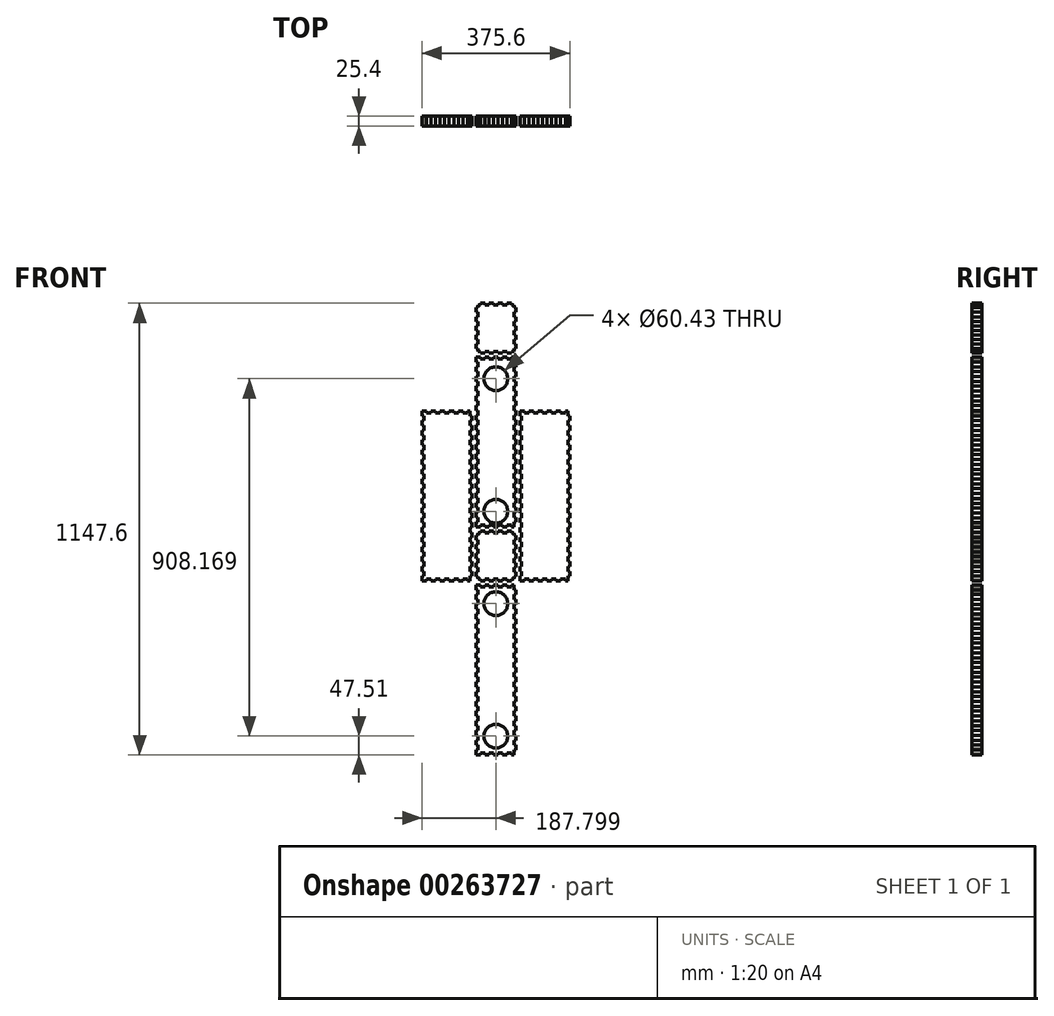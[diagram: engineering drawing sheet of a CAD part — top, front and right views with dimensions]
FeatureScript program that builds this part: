
annotation { "Feature Type Name" : "Feature", "Feature Type Description" : "" }
export const myFeature = defineFeature(function(context is Context, id is Id, definition is map)
    precondition{}
    {
        {
            var Q0;
            Q0=qCreatedBy(makeId("Front.planeOp"),FACE);
            var sketch = newSketch(context, id + "F0", { "sketchPlane" : qUnion([Q0])});
            skLineSegment(sketch, "E0", {"start": v(-50.8, -573.8) * mm, "end": v(-39.51, -573.8) * mm});
            skLineSegment(sketch, "E1", {"start": v(-39.51, -569.04) * mm, "end": v(-39.51, -573.8) * mm});
            skLineSegment(sketch, "E2", {"start": v(-39.51, -569.04) * mm, "end": v(-28.22, -569.04) * mm});
            skLineSegment(sketch, "E3", {"start": v(-28.22, -569.04) * mm, "end": v(-28.22, -573.8) * mm});
            skLineSegment(sketch, "E4", {"start": v(-28.22, -573.8) * mm, "end": v(-16.93, -573.8) * mm});
            skLineSegment(sketch, "E5", {"start": v(-16.93, -569.04) * mm, "end": v(-16.93, -573.8) * mm});
            skLineSegment(sketch, "E6", {"start": v(-16.93, -569.04) * mm, "end": v(-5.65, -569.04) * mm});
            skLineSegment(sketch, "E7", {"start": v(-5.65, -569.04) * mm, "end": v(-5.65, -573.8) * mm});
            skLineSegment(sketch, "E8", {"start": v(-5.65, -573.8) * mm, "end": v(5.64, -573.8) * mm});
            skLineSegment(sketch, "E9", {"start": v(5.64, -569.04) * mm, "end": v(5.64, -573.8) * mm});
            skLineSegment(sketch, "E10", {"start": v(5.64, -569.04) * mm, "end": v(16.93, -569.04) * mm});
            skLineSegment(sketch, "E11", {"start": v(16.93, -569.04) * mm, "end": v(16.93, -573.8) * mm});
            skLineSegment(sketch, "E12", {"start": v(16.93, -573.8) * mm, "end": v(28.22, -573.8) * mm});
            skLineSegment(sketch, "E13", {"start": v(28.22, -569.04) * mm, "end": v(28.22, -573.8) * mm});
            skLineSegment(sketch, "E14", {"start": v(28.22, -569.04) * mm, "end": v(39.51, -569.04) * mm});
            skLineSegment(sketch, "E15", {"start": v(39.51, -569.04) * mm, "end": v(39.51, -573.8) * mm});
            skLineSegment(sketch, "E16", {"start": v(39.51, -573.8) * mm, "end": v(46.04, -573.8) * mm});
            skLineSegment(sketch, "E17", {"start": v(-50.8, -142) * mm, "end": v(-39.51, -142) * mm});
            skLineSegment(sketch, "E18", {"start": v(-39.51, -142) * mm, "end": v(-39.51, -146.76) * mm});
            skLineSegment(sketch, "E19", {"start": v(-39.51, -146.76) * mm, "end": v(-28.22, -146.76) * mm});
            skLineSegment(sketch, "E20", {"start": v(-28.22, -142) * mm, "end": v(-28.22, -146.76) * mm});
            skLineSegment(sketch, "E21", {"start": v(-28.22, -142) * mm, "end": v(-16.93, -142) * mm});
            skLineSegment(sketch, "E22", {"start": v(-16.93, -142) * mm, "end": v(-16.93, -146.76) * mm});
            skLineSegment(sketch, "E23", {"start": v(-16.93, -146.76) * mm, "end": v(-5.65, -146.76) * mm});
            skLineSegment(sketch, "E24", {"start": v(-5.65, -142) * mm, "end": v(-5.65, -146.76) * mm});
            skLineSegment(sketch, "E25", {"start": v(-5.65, -142) * mm, "end": v(5.64, -142) * mm});
            skLineSegment(sketch, "E26", {"start": v(5.64, -142) * mm, "end": v(5.64, -146.76) * mm});
            skLineSegment(sketch, "E27", {"start": v(5.64, -146.76) * mm, "end": v(16.93, -146.76) * mm});
            skLineSegment(sketch, "E28", {"start": v(16.93, -142) * mm, "end": v(16.93, -146.76) * mm});
            skLineSegment(sketch, "E29", {"start": v(16.93, -142) * mm, "end": v(28.22, -142) * mm});
            skLineSegment(sketch, "E30", {"start": v(28.22, -142) * mm, "end": v(28.22, -146.76) * mm});
            skLineSegment(sketch, "E31", {"start": v(28.22, -146.76) * mm, "end": v(39.51, -146.76) * mm});
            skLineSegment(sketch, "E32", {"start": v(39.51, -142) * mm, "end": v(39.51, -146.76) * mm});
            skLineSegment(sketch, "E33", {"start": v(39.51, -142) * mm, "end": v(46.04, -142) * mm});
            skLineSegment(sketch, "E34", {"start": v(-50.8, -573.8) * mm, "end": v(-50.8, -561.46) * mm});
            skLineSegment(sketch, "E35", {"start": v(-46.04, -561.46) * mm, "end": v(-50.8, -561.46) * mm});
            skLineSegment(sketch, "E36", {"start": v(-46.04, -561.46) * mm, "end": v(-46.04, -549.13) * mm});
            skLineSegment(sketch, "E37", {"start": v(-46.04, -549.13) * mm, "end": v(-50.8, -549.13) * mm});
            skLineSegment(sketch, "E38", {"start": v(-50.8, -549.13) * mm, "end": v(-50.8, -536.79) * mm});
            skLineSegment(sketch, "E39", {"start": v(-46.04, -536.79) * mm, "end": v(-50.8, -536.79) * mm});
            skLineSegment(sketch, "E40", {"start": v(-46.04, -536.79) * mm, "end": v(-46.04, -524.45) * mm});
            skLineSegment(sketch, "E41", {"start": v(-46.04, -524.45) * mm, "end": v(-50.8, -524.45) * mm});
            skLineSegment(sketch, "E42", {"start": v(-50.8, -524.45) * mm, "end": v(-50.8, -512.12) * mm});
            skLineSegment(sketch, "E43", {"start": v(-46.04, -512.12) * mm, "end": v(-50.8, -512.12) * mm});
            skLineSegment(sketch, "E44", {"start": v(-46.04, -512.12) * mm, "end": v(-46.04, -499.78) * mm});
            skLineSegment(sketch, "E45", {"start": v(-46.04, -499.78) * mm, "end": v(-50.8, -499.78) * mm});
            skLineSegment(sketch, "E46", {"start": v(-50.8, -499.78) * mm, "end": v(-50.8, -487.44) * mm});
            skLineSegment(sketch, "E47", {"start": v(-46.04, -487.44) * mm, "end": v(-50.8, -487.44) * mm});
            skLineSegment(sketch, "E48", {"start": v(-46.04, -487.44) * mm, "end": v(-46.04, -475.1) * mm});
            skLineSegment(sketch, "E49", {"start": v(-46.04, -475.1) * mm, "end": v(-50.8, -475.1) * mm});
            skLineSegment(sketch, "E50", {"start": v(-50.8, -475.1) * mm, "end": v(-50.8, -462.77) * mm});
            skLineSegment(sketch, "E51", {"start": v(-46.04, -462.77) * mm, "end": v(-50.8, -462.77) * mm});
            skLineSegment(sketch, "E52", {"start": v(-46.04, -462.77) * mm, "end": v(-46.04, -450.43) * mm});
            skLineSegment(sketch, "E53", {"start": v(-46.04, -450.43) * mm, "end": v(-50.8, -450.43) * mm});
            skLineSegment(sketch, "E54", {"start": v(-50.8, -450.43) * mm, "end": v(-50.8, -438.1) * mm});
            skLineSegment(sketch, "E55", {"start": v(-46.04, -438.1) * mm, "end": v(-50.8, -438.1) * mm});
            skLineSegment(sketch, "E56", {"start": v(-46.04, -438.1) * mm, "end": v(-46.04, -425.76) * mm});
            skLineSegment(sketch, "E57", {"start": v(-46.04, -425.76) * mm, "end": v(-50.8, -425.76) * mm});
            skLineSegment(sketch, "E58", {"start": v(-50.8, -425.76) * mm, "end": v(-50.8, -413.42) * mm});
            skLineSegment(sketch, "E59", {"start": v(-46.04, -413.42) * mm, "end": v(-50.8, -413.42) * mm});
            skLineSegment(sketch, "E60", {"start": v(-46.04, -413.42) * mm, "end": v(-46.04, -401.08) * mm});
            skLineSegment(sketch, "E61", {"start": v(-46.04, -401.08) * mm, "end": v(-50.8, -401.08) * mm});
            skLineSegment(sketch, "E62", {"start": v(-50.8, -401.08) * mm, "end": v(-50.8, -388.74) * mm});
            skLineSegment(sketch, "E63", {"start": v(-46.04, -388.74) * mm, "end": v(-50.8, -388.74) * mm});
            skLineSegment(sketch, "E64", {"start": v(-46.04, -388.74) * mm, "end": v(-46.04, -376.4) * mm});
            skLineSegment(sketch, "E65", {"start": v(-46.04, -376.4) * mm, "end": v(-50.8, -376.4) * mm});
            skLineSegment(sketch, "E66", {"start": v(-50.8, -376.4) * mm, "end": v(-50.8, -364.07) * mm});
            skLineSegment(sketch, "E67", {"start": v(-46.04, -364.07) * mm, "end": v(-50.8, -364.07) * mm});
            skLineSegment(sketch, "E68", {"start": v(-46.04, -364.07) * mm, "end": v(-46.04, -351.73) * mm});
            skLineSegment(sketch, "E69", {"start": v(-46.04, -351.73) * mm, "end": v(-50.8, -351.73) * mm});
            skLineSegment(sketch, "E70", {"start": v(-50.8, -351.73) * mm, "end": v(-50.8, -339.4) * mm});
            skLineSegment(sketch, "E71", {"start": v(-46.04, -339.4) * mm, "end": v(-50.8, -339.4) * mm});
            skLineSegment(sketch, "E72", {"start": v(-46.04, -339.4) * mm, "end": v(-46.04, -327.06) * mm});
            skLineSegment(sketch, "E73", {"start": v(-46.04, -327.06) * mm, "end": v(-50.8, -327.06) * mm});
            skLineSegment(sketch, "E74", {"start": v(-50.8, -327.06) * mm, "end": v(-50.8, -314.72) * mm});
            skLineSegment(sketch, "E75", {"start": v(-46.04, -314.72) * mm, "end": v(-50.8, -314.72) * mm});
            skLineSegment(sketch, "E76", {"start": v(-46.04, -314.72) * mm, "end": v(-46.04, -302.38) * mm});
            skLineSegment(sketch, "E77", {"start": v(-46.04, -302.38) * mm, "end": v(-50.8, -302.38) * mm});
            skLineSegment(sketch, "E78", {"start": v(-50.8, -302.38) * mm, "end": v(-50.8, -290.05) * mm});
            skLineSegment(sketch, "E79", {"start": v(-46.04, -290.05) * mm, "end": v(-50.8, -290.05) * mm});
            skLineSegment(sketch, "E80", {"start": v(-46.04, -290.05) * mm, "end": v(-46.04, -277.71) * mm});
            skLineSegment(sketch, "E81", {"start": v(-46.04, -277.71) * mm, "end": v(-50.8, -277.71) * mm});
            skLineSegment(sketch, "E82", {"start": v(-50.8, -277.71) * mm, "end": v(-50.8, -265.37) * mm});
            skLineSegment(sketch, "E83", {"start": v(-46.04, -265.37) * mm, "end": v(-50.8, -265.37) * mm});
            skLineSegment(sketch, "E84", {"start": v(-46.04, -265.37) * mm, "end": v(-46.04, -253.04) * mm});
            skLineSegment(sketch, "E85", {"start": v(-46.04, -253.04) * mm, "end": v(-50.8, -253.04) * mm});
            skLineSegment(sketch, "E86", {"start": v(-50.8, -253.04) * mm, "end": v(-50.8, -240.7) * mm});
            skLineSegment(sketch, "E87", {"start": v(-46.04, -240.7) * mm, "end": v(-50.8, -240.7) * mm});
            skLineSegment(sketch, "E88", {"start": v(-46.04, -240.7) * mm, "end": v(-46.04, -228.36) * mm});
            skLineSegment(sketch, "E89", {"start": v(-46.04, -228.36) * mm, "end": v(-50.8, -228.36) * mm});
            skLineSegment(sketch, "E90", {"start": v(-50.8, -228.36) * mm, "end": v(-50.8, -216.02) * mm});
            skLineSegment(sketch, "E91", {"start": v(-46.04, -216.02) * mm, "end": v(-50.8, -216.02) * mm});
            skLineSegment(sketch, "E92", {"start": v(-46.04, -216.02) * mm, "end": v(-46.04, -203.69) * mm});
            skLineSegment(sketch, "E93", {"start": v(-46.04, -203.69) * mm, "end": v(-50.8, -203.69) * mm});
            skLineSegment(sketch, "E94", {"start": v(-50.8, -203.69) * mm, "end": v(-50.8, -191.35) * mm});
            skLineSegment(sketch, "E95", {"start": v(-46.04, -191.35) * mm, "end": v(-50.8, -191.35) * mm});
            skLineSegment(sketch, "E96", {"start": v(-46.04, -191.35) * mm, "end": v(-46.04, -179.01) * mm});
            skLineSegment(sketch, "E97", {"start": v(-46.04, -179.01) * mm, "end": v(-50.8, -179.01) * mm});
            skLineSegment(sketch, "E98", {"start": v(-50.8, -179.01) * mm, "end": v(-50.8, -166.68) * mm});
            skLineSegment(sketch, "E99", {"start": v(-46.04, -166.68) * mm, "end": v(-50.8, -166.68) * mm});
            skLineSegment(sketch, "E100", {"start": v(-46.04, -166.68) * mm, "end": v(-46.04, -154.34) * mm});
            skLineSegment(sketch, "E101", {"start": v(-46.04, -154.34) * mm, "end": v(-50.8, -154.34) * mm});
            skLineSegment(sketch, "E102", {"start": v(-50.8, -154.34) * mm, "end": v(-50.8, -142) * mm});
            skLineSegment(sketch, "E103", {"start": v(46.04, -573.8) * mm, "end": v(46.04, -561.46) * mm});
            skLineSegment(sketch, "E104", {"start": v(50.8, -561.46) * mm, "end": v(46.04, -561.46) * mm});
            skLineSegment(sketch, "E105", {"start": v(50.8, -561.46) * mm, "end": v(50.8, -549.13) * mm});
            skLineSegment(sketch, "E106", {"start": v(50.8, -549.13) * mm, "end": v(46.04, -549.13) * mm});
            skLineSegment(sketch, "E107", {"start": v(46.04, -549.13) * mm, "end": v(46.04, -536.79) * mm});
            skLineSegment(sketch, "E108", {"start": v(50.8, -536.79) * mm, "end": v(46.04, -536.79) * mm});
            skLineSegment(sketch, "E109", {"start": v(50.8, -536.79) * mm, "end": v(50.8, -524.45) * mm});
            skLineSegment(sketch, "E110", {"start": v(50.8, -524.45) * mm, "end": v(46.04, -524.45) * mm});
            skLineSegment(sketch, "E111", {"start": v(46.04, -524.45) * mm, "end": v(46.04, -512.12) * mm});
            skLineSegment(sketch, "E112", {"start": v(50.8, -512.12) * mm, "end": v(46.04, -512.12) * mm});
            skLineSegment(sketch, "E113", {"start": v(50.8, -512.12) * mm, "end": v(50.8, -499.78) * mm});
            skLineSegment(sketch, "E114", {"start": v(50.8, -499.78) * mm, "end": v(46.04, -499.78) * mm});
            skLineSegment(sketch, "E115", {"start": v(46.04, -499.78) * mm, "end": v(46.04, -487.44) * mm});
            skLineSegment(sketch, "E116", {"start": v(50.8, -487.44) * mm, "end": v(46.04, -487.44) * mm});
            skLineSegment(sketch, "E117", {"start": v(50.8, -487.44) * mm, "end": v(50.8, -475.1) * mm});
            skLineSegment(sketch, "E118", {"start": v(50.8, -475.1) * mm, "end": v(46.04, -475.1) * mm});
            skLineSegment(sketch, "E119", {"start": v(46.04, -475.1) * mm, "end": v(46.04, -462.77) * mm});
            skLineSegment(sketch, "E120", {"start": v(50.8, -462.77) * mm, "end": v(46.04, -462.77) * mm});
            skLineSegment(sketch, "E121", {"start": v(50.8, -462.77) * mm, "end": v(50.8, -450.43) * mm});
            skLineSegment(sketch, "E122", {"start": v(50.8, -450.43) * mm, "end": v(46.04, -450.43) * mm});
            skLineSegment(sketch, "E123", {"start": v(46.04, -450.43) * mm, "end": v(46.04, -438.1) * mm});
            skLineSegment(sketch, "E124", {"start": v(50.8, -438.1) * mm, "end": v(46.04, -438.1) * mm});
            skLineSegment(sketch, "E125", {"start": v(50.8, -438.1) * mm, "end": v(50.8, -425.76) * mm});
            skLineSegment(sketch, "E126", {"start": v(50.8, -425.76) * mm, "end": v(46.04, -425.76) * mm});
            skLineSegment(sketch, "E127", {"start": v(46.04, -425.76) * mm, "end": v(46.04, -413.42) * mm});
            skLineSegment(sketch, "E128", {"start": v(50.8, -413.42) * mm, "end": v(46.04, -413.42) * mm});
            skLineSegment(sketch, "E129", {"start": v(50.8, -413.42) * mm, "end": v(50.8, -401.08) * mm});
            skLineSegment(sketch, "E130", {"start": v(50.8, -401.08) * mm, "end": v(46.04, -401.08) * mm});
            skLineSegment(sketch, "E131", {"start": v(46.04, -401.08) * mm, "end": v(46.04, -388.74) * mm});
            skLineSegment(sketch, "E132", {"start": v(50.8, -388.74) * mm, "end": v(46.04, -388.74) * mm});
            skLineSegment(sketch, "E133", {"start": v(50.8, -388.74) * mm, "end": v(50.8, -376.4) * mm});
            skLineSegment(sketch, "E134", {"start": v(50.8, -376.4) * mm, "end": v(46.04, -376.4) * mm});
            skLineSegment(sketch, "E135", {"start": v(46.04, -376.4) * mm, "end": v(46.04, -364.07) * mm});
            skLineSegment(sketch, "E136", {"start": v(50.8, -364.07) * mm, "end": v(46.04, -364.07) * mm});
            skLineSegment(sketch, "E137", {"start": v(50.8, -364.07) * mm, "end": v(50.8, -351.73) * mm});
            skLineSegment(sketch, "E138", {"start": v(50.8, -351.73) * mm, "end": v(46.04, -351.73) * mm});
            skLineSegment(sketch, "E139", {"start": v(46.04, -351.73) * mm, "end": v(46.04, -339.4) * mm});
            skLineSegment(sketch, "E140", {"start": v(50.8, -339.4) * mm, "end": v(46.04, -339.4) * mm});
            skLineSegment(sketch, "E141", {"start": v(50.8, -339.4) * mm, "end": v(50.8, -327.06) * mm});
            skLineSegment(sketch, "E142", {"start": v(50.8, -327.06) * mm, "end": v(46.04, -327.06) * mm});
            skLineSegment(sketch, "E143", {"start": v(46.04, -327.06) * mm, "end": v(46.04, -314.72) * mm});
            skLineSegment(sketch, "E144", {"start": v(50.8, -314.72) * mm, "end": v(46.04, -314.72) * mm});
            skLineSegment(sketch, "E145", {"start": v(50.8, -314.72) * mm, "end": v(50.8, -302.38) * mm});
            skLineSegment(sketch, "E146", {"start": v(50.8, -302.38) * mm, "end": v(46.04, -302.38) * mm});
            skLineSegment(sketch, "E147", {"start": v(46.04, -302.38) * mm, "end": v(46.04, -290.05) * mm});
            skLineSegment(sketch, "E148", {"start": v(50.8, -290.05) * mm, "end": v(46.04, -290.05) * mm});
            skLineSegment(sketch, "E149", {"start": v(50.8, -290.05) * mm, "end": v(50.8, -277.71) * mm});
            skLineSegment(sketch, "E150", {"start": v(50.8, -277.71) * mm, "end": v(46.04, -277.71) * mm});
            skLineSegment(sketch, "E151", {"start": v(46.04, -277.71) * mm, "end": v(46.04, -265.37) * mm});
            skLineSegment(sketch, "E152", {"start": v(50.8, -265.37) * mm, "end": v(46.04, -265.37) * mm});
            skLineSegment(sketch, "E153", {"start": v(50.8, -265.37) * mm, "end": v(50.8, -253.04) * mm});
            skLineSegment(sketch, "E154", {"start": v(50.8, -253.04) * mm, "end": v(46.04, -253.04) * mm});
            skLineSegment(sketch, "E155", {"start": v(46.04, -253.04) * mm, "end": v(46.04, -240.7) * mm});
            skLineSegment(sketch, "E156", {"start": v(50.8, -240.7) * mm, "end": v(46.04, -240.7) * mm});
            skLineSegment(sketch, "E157", {"start": v(50.8, -240.7) * mm, "end": v(50.8, -228.36) * mm});
            skLineSegment(sketch, "E158", {"start": v(50.8, -228.36) * mm, "end": v(46.04, -228.36) * mm});
            skLineSegment(sketch, "E159", {"start": v(46.04, -228.36) * mm, "end": v(46.04, -216.02) * mm});
            skLineSegment(sketch, "E160", {"start": v(50.8, -216.02) * mm, "end": v(46.04, -216.02) * mm});
            skLineSegment(sketch, "E161", {"start": v(50.8, -216.02) * mm, "end": v(50.8, -203.69) * mm});
            skLineSegment(sketch, "E162", {"start": v(50.8, -203.69) * mm, "end": v(46.04, -203.69) * mm});
            skLineSegment(sketch, "E163", {"start": v(46.04, -203.69) * mm, "end": v(46.04, -191.35) * mm});
            skLineSegment(sketch, "E164", {"start": v(50.8, -191.35) * mm, "end": v(46.04, -191.35) * mm});
            skLineSegment(sketch, "E165", {"start": v(50.8, -191.35) * mm, "end": v(50.8, -179.01) * mm});
            skLineSegment(sketch, "E166", {"start": v(50.8, -179.01) * mm, "end": v(46.04, -179.01) * mm});
            skLineSegment(sketch, "E167", {"start": v(46.04, -179.01) * mm, "end": v(46.04, -166.68) * mm});
            skLineSegment(sketch, "E168", {"start": v(50.8, -166.68) * mm, "end": v(46.04, -166.68) * mm});
            skLineSegment(sketch, "E169", {"start": v(50.8, -166.68) * mm, "end": v(50.8, -154.34) * mm});
            skLineSegment(sketch, "E170", {"start": v(50.8, -154.34) * mm, "end": v(46.04, -154.34) * mm});
            skLineSegment(sketch, "E171", {"start": v(46.04, -154.34) * mm, "end": v(46.04, -142) * mm});
            skLineSegment(sketch, "E172", {"start": v(-187.8, -132) * mm, "end": v(-176.25, -132) * mm});
            skLineSegment(sketch, "E173", {"start": v(-176.25, -127.24) * mm, "end": v(-176.25, -132) * mm});
            skLineSegment(sketch, "E174", {"start": v(-176.25, -127.24) * mm, "end": v(-164.7, -127.24) * mm});
            skLineSegment(sketch, "E175", {"start": v(-164.7, -127.24) * mm, "end": v(-164.7, -132) * mm});
            skLineSegment(sketch, "E176", {"start": v(-164.7, -132) * mm, "end": v(-153.16, -132) * mm});
            skLineSegment(sketch, "E177", {"start": v(-153.16, -127.24) * mm, "end": v(-153.16, -132) * mm});
            skLineSegment(sketch, "E178", {"start": v(-153.16, -127.24) * mm, "end": v(-141.62, -127.24) * mm});
            skLineSegment(sketch, "E179", {"start": v(-141.62, -127.24) * mm, "end": v(-141.62, -132) * mm});
            skLineSegment(sketch, "E180", {"start": v(-141.62, -132) * mm, "end": v(-130.07, -132) * mm});
            skLineSegment(sketch, "E181", {"start": v(-130.07, -127.24) * mm, "end": v(-130.07, -132) * mm});
            skLineSegment(sketch, "E182", {"start": v(-130.07, -127.24) * mm, "end": v(-118.53, -127.24) * mm});
            skLineSegment(sketch, "E183", {"start": v(-118.53, -127.24) * mm, "end": v(-118.53, -132) * mm});
            skLineSegment(sketch, "E184", {"start": v(-118.53, -132) * mm, "end": v(-106.98, -132) * mm});
            skLineSegment(sketch, "E185", {"start": v(-106.98, -127.24) * mm, "end": v(-106.98, -132) * mm});
            skLineSegment(sketch, "E186", {"start": v(-106.98, -127.24) * mm, "end": v(-95.44, -127.24) * mm});
            skLineSegment(sketch, "E187", {"start": v(-95.44, -127.24) * mm, "end": v(-95.44, -132) * mm});
            skLineSegment(sketch, "E188", {"start": v(-95.44, -132) * mm, "end": v(-83.9, -132) * mm});
            skLineSegment(sketch, "E189", {"start": v(-83.9, -127.24) * mm, "end": v(-83.9, -132) * mm});
            skLineSegment(sketch, "E190", {"start": v(-83.9, -127.24) * mm, "end": v(-72.35, -127.24) * mm});
            skLineSegment(sketch, "E191", {"start": v(-72.35, -127.24) * mm, "end": v(-72.35, -132) * mm});
            skLineSegment(sketch, "E192", {"start": v(-72.35, -132) * mm, "end": v(-65.56, -132) * mm});
            skLineSegment(sketch, "E193", {"start": v(-187.8, 299.8) * mm, "end": v(-176.25, 299.8) * mm});
            skLineSegment(sketch, "E194", {"start": v(-176.25, 299.8) * mm, "end": v(-176.25, 295.04) * mm});
            skLineSegment(sketch, "E195", {"start": v(-176.25, 295.04) * mm, "end": v(-164.7, 295.04) * mm});
            skLineSegment(sketch, "E196", {"start": v(-164.7, 299.8) * mm, "end": v(-164.7, 295.04) * mm});
            skLineSegment(sketch, "E197", {"start": v(-164.7, 299.8) * mm, "end": v(-153.16, 299.8) * mm});
            skLineSegment(sketch, "E198", {"start": v(-153.16, 299.8) * mm, "end": v(-153.16, 295.04) * mm});
            skLineSegment(sketch, "E199", {"start": v(-153.16, 295.04) * mm, "end": v(-141.62, 295.04) * mm});
            skLineSegment(sketch, "E200", {"start": v(-141.62, 299.8) * mm, "end": v(-141.62, 295.04) * mm});
            skLineSegment(sketch, "E201", {"start": v(-141.62, 299.8) * mm, "end": v(-130.07, 299.8) * mm});
            skLineSegment(sketch, "E202", {"start": v(-130.07, 299.8) * mm, "end": v(-130.07, 295.04) * mm});
            skLineSegment(sketch, "E203", {"start": v(-130.07, 295.04) * mm, "end": v(-118.53, 295.04) * mm});
            skLineSegment(sketch, "E204", {"start": v(-118.53, 299.8) * mm, "end": v(-118.53, 295.04) * mm});
            skLineSegment(sketch, "E205", {"start": v(-118.53, 299.8) * mm, "end": v(-106.98, 299.8) * mm});
            skLineSegment(sketch, "E206", {"start": v(-106.98, 299.8) * mm, "end": v(-106.98, 295.04) * mm});
            skLineSegment(sketch, "E207", {"start": v(-106.98, 295.04) * mm, "end": v(-95.44, 295.04) * mm});
            skLineSegment(sketch, "E208", {"start": v(-95.44, 299.8) * mm, "end": v(-95.44, 295.04) * mm});
            skLineSegment(sketch, "E209", {"start": v(-95.44, 299.8) * mm, "end": v(-83.9, 299.8) * mm});
            skLineSegment(sketch, "E210", {"start": v(-83.9, 299.8) * mm, "end": v(-83.9, 295.04) * mm});
            skLineSegment(sketch, "E211", {"start": v(-83.9, 295.04) * mm, "end": v(-72.35, 295.04) * mm});
            skLineSegment(sketch, "E212", {"start": v(-72.35, 299.8) * mm, "end": v(-72.35, 295.04) * mm});
            skLineSegment(sketch, "E213", {"start": v(-72.35, 299.8) * mm, "end": v(-65.56, 299.8) * mm});
            skLineSegment(sketch, "E214", {"start": v(-187.8, -132) * mm, "end": v(-187.8, -119.66) * mm});
            skLineSegment(sketch, "E215", {"start": v(-183.04, -119.66) * mm, "end": v(-187.8, -119.66) * mm});
            skLineSegment(sketch, "E216", {"start": v(-183.04, -119.66) * mm, "end": v(-183.04, -107.33) * mm});
            skLineSegment(sketch, "E217", {"start": v(-183.04, -107.33) * mm, "end": v(-187.8, -107.33) * mm});
            skLineSegment(sketch, "E218", {"start": v(-187.8, -107.33) * mm, "end": v(-187.8, -94.99) * mm});
            skLineSegment(sketch, "E219", {"start": v(-183.04, -94.99) * mm, "end": v(-187.8, -94.99) * mm});
            skLineSegment(sketch, "E220", {"start": v(-183.04, -94.99) * mm, "end": v(-183.04, -82.65) * mm});
            skLineSegment(sketch, "E221", {"start": v(-183.04, -82.65) * mm, "end": v(-187.8, -82.65) * mm});
            skLineSegment(sketch, "E222", {"start": v(-187.8, -82.65) * mm, "end": v(-187.8, -70.32) * mm});
            skLineSegment(sketch, "E223", {"start": v(-183.04, -70.32) * mm, "end": v(-187.8, -70.32) * mm});
            skLineSegment(sketch, "E224", {"start": v(-183.04, -70.32) * mm, "end": v(-183.04, -57.98) * mm});
            skLineSegment(sketch, "E225", {"start": v(-183.04, -57.98) * mm, "end": v(-187.8, -57.98) * mm});
            skLineSegment(sketch, "E226", {"start": v(-187.8, -57.98) * mm, "end": v(-187.8, -45.64) * mm});
            skLineSegment(sketch, "E227", {"start": v(-183.04, -45.64) * mm, "end": v(-187.8, -45.64) * mm});
            skLineSegment(sketch, "E228", {"start": v(-183.04, -45.64) * mm, "end": v(-183.04, -33.3) * mm});
            skLineSegment(sketch, "E229", {"start": v(-183.04, -33.3) * mm, "end": v(-187.8, -33.3) * mm});
            skLineSegment(sketch, "E230", {"start": v(-187.8, -33.3) * mm, "end": v(-187.8, -20.97) * mm});
            skLineSegment(sketch, "E231", {"start": v(-183.04, -20.97) * mm, "end": v(-187.8, -20.97) * mm});
            skLineSegment(sketch, "E232", {"start": v(-183.04, -20.97) * mm, "end": v(-183.04, -8.63) * mm});
            skLineSegment(sketch, "E233", {"start": v(-183.04, -8.63) * mm, "end": v(-187.8, -8.63) * mm});
            skLineSegment(sketch, "E234", {"start": v(-187.8, -8.63) * mm, "end": v(-187.8, 3.7) * mm});
            skLineSegment(sketch, "E235", {"start": v(-183.04, 3.7) * mm, "end": v(-187.8, 3.7) * mm});
            skLineSegment(sketch, "E236", {"start": v(-183.04, 3.7) * mm, "end": v(-183.04, 16.04) * mm});
            skLineSegment(sketch, "E237", {"start": v(-183.04, 16.04) * mm, "end": v(-187.8, 16.04) * mm});
            skLineSegment(sketch, "E238", {"start": v(-187.8, 16.04) * mm, "end": v(-187.8, 28.38) * mm});
            skLineSegment(sketch, "E239", {"start": v(-183.04, 28.38) * mm, "end": v(-187.8, 28.38) * mm});
            skLineSegment(sketch, "E240", {"start": v(-183.04, 28.38) * mm, "end": v(-183.04, 40.72) * mm});
            skLineSegment(sketch, "E241", {"start": v(-183.04, 40.72) * mm, "end": v(-187.8, 40.72) * mm});
            skLineSegment(sketch, "E242", {"start": v(-187.8, 40.72) * mm, "end": v(-187.8, 53.06) * mm});
            skLineSegment(sketch, "E243", {"start": v(-183.04, 53.06) * mm, "end": v(-187.8, 53.06) * mm});
            skLineSegment(sketch, "E244", {"start": v(-183.04, 53.06) * mm, "end": v(-183.04, 65.39) * mm});
            skLineSegment(sketch, "E245", {"start": v(-183.04, 65.39) * mm, "end": v(-187.8, 65.39) * mm});
            skLineSegment(sketch, "E246", {"start": v(-187.8, 65.39) * mm, "end": v(-187.8, 77.73) * mm});
            skLineSegment(sketch, "E247", {"start": v(-183.04, 77.73) * mm, "end": v(-187.8, 77.73) * mm});
            skLineSegment(sketch, "E248", {"start": v(-183.04, 77.73) * mm, "end": v(-183.04, 90.07) * mm});
            skLineSegment(sketch, "E249", {"start": v(-183.04, 90.07) * mm, "end": v(-187.8, 90.07) * mm});
            skLineSegment(sketch, "E250", {"start": v(-187.8, 90.07) * mm, "end": v(-187.8, 102.4) * mm});
            skLineSegment(sketch, "E251", {"start": v(-183.04, 102.4) * mm, "end": v(-187.8, 102.4) * mm});
            skLineSegment(sketch, "E252", {"start": v(-183.04, 102.4) * mm, "end": v(-183.04, 114.74) * mm});
            skLineSegment(sketch, "E253", {"start": v(-183.04, 114.74) * mm, "end": v(-187.8, 114.74) * mm});
            skLineSegment(sketch, "E254", {"start": v(-187.8, 114.74) * mm, "end": v(-187.8, 127.08) * mm});
            skLineSegment(sketch, "E255", {"start": v(-183.04, 127.08) * mm, "end": v(-187.8, 127.08) * mm});
            skLineSegment(sketch, "E256", {"start": v(-183.04, 127.08) * mm, "end": v(-183.04, 139.42) * mm});
            skLineSegment(sketch, "E257", {"start": v(-183.04, 139.42) * mm, "end": v(-187.8, 139.42) * mm});
            skLineSegment(sketch, "E258", {"start": v(-187.8, 139.42) * mm, "end": v(-187.8, 151.75) * mm});
            skLineSegment(sketch, "E259", {"start": v(-183.04, 151.75) * mm, "end": v(-187.8, 151.75) * mm});
            skLineSegment(sketch, "E260", {"start": v(-183.04, 151.75) * mm, "end": v(-183.04, 164.1) * mm});
            skLineSegment(sketch, "E261", {"start": v(-183.04, 164.1) * mm, "end": v(-187.8, 164.1) * mm});
            skLineSegment(sketch, "E262", {"start": v(-187.8, 164.1) * mm, "end": v(-187.8, 176.43) * mm});
            skLineSegment(sketch, "E263", {"start": v(-183.04, 176.43) * mm, "end": v(-187.8, 176.43) * mm});
            skLineSegment(sketch, "E264", {"start": v(-183.04, 176.43) * mm, "end": v(-183.04, 188.76) * mm});
            skLineSegment(sketch, "E265", {"start": v(-183.04, 188.76) * mm, "end": v(-187.8, 188.76) * mm});
            skLineSegment(sketch, "E266", {"start": v(-187.8, 188.76) * mm, "end": v(-187.8, 201.1) * mm});
            skLineSegment(sketch, "E267", {"start": v(-183.04, 201.1) * mm, "end": v(-187.8, 201.1) * mm});
            skLineSegment(sketch, "E268", {"start": v(-183.04, 201.1) * mm, "end": v(-183.04, 213.44) * mm});
            skLineSegment(sketch, "E269", {"start": v(-183.04, 213.44) * mm, "end": v(-187.8, 213.44) * mm});
            skLineSegment(sketch, "E270", {"start": v(-187.8, 213.44) * mm, "end": v(-187.8, 225.78) * mm});
            skLineSegment(sketch, "E271", {"start": v(-183.04, 225.78) * mm, "end": v(-187.8, 225.78) * mm});
            skLineSegment(sketch, "E272", {"start": v(-183.04, 225.78) * mm, "end": v(-183.04, 238.11) * mm});
            skLineSegment(sketch, "E273", {"start": v(-183.04, 238.11) * mm, "end": v(-187.8, 238.11) * mm});
            skLineSegment(sketch, "E274", {"start": v(-187.8, 238.11) * mm, "end": v(-187.8, 250.45) * mm});
            skLineSegment(sketch, "E275", {"start": v(-183.04, 250.45) * mm, "end": v(-187.8, 250.45) * mm});
            skLineSegment(sketch, "E276", {"start": v(-183.04, 250.45) * mm, "end": v(-183.04, 262.79) * mm});
            skLineSegment(sketch, "E277", {"start": v(-183.04, 262.79) * mm, "end": v(-187.8, 262.79) * mm});
            skLineSegment(sketch, "E278", {"start": v(-187.8, 262.79) * mm, "end": v(-187.8, 275.12) * mm});
            skLineSegment(sketch, "E279", {"start": v(-183.04, 275.12) * mm, "end": v(-187.8, 275.12) * mm});
            skLineSegment(sketch, "E280", {"start": v(-183.04, 275.12) * mm, "end": v(-183.04, 287.46) * mm});
            skLineSegment(sketch, "E281", {"start": v(-183.04, 287.46) * mm, "end": v(-187.8, 287.46) * mm});
            skLineSegment(sketch, "E282", {"start": v(-187.8, 287.46) * mm, "end": v(-187.8, 299.8) * mm});
            skLineSegment(sketch, "E283", {"start": v(-65.56, -132) * mm, "end": v(-65.56, -119.66) * mm});
            skLineSegment(sketch, "E284", {"start": v(-60.8, -119.66) * mm, "end": v(-65.56, -119.66) * mm});
            skLineSegment(sketch, "E285", {"start": v(-60.8, -119.66) * mm, "end": v(-60.8, -107.33) * mm});
            skLineSegment(sketch, "E286", {"start": v(-60.8, -107.33) * mm, "end": v(-65.56, -107.33) * mm});
            skLineSegment(sketch, "E287", {"start": v(-65.56, -107.33) * mm, "end": v(-65.56, -94.99) * mm});
            skLineSegment(sketch, "E288", {"start": v(-60.8, -94.99) * mm, "end": v(-65.56, -94.99) * mm});
            skLineSegment(sketch, "E289", {"start": v(-60.8, -94.99) * mm, "end": v(-60.8, -82.65) * mm});
            skLineSegment(sketch, "E290", {"start": v(-60.8, -82.65) * mm, "end": v(-65.56, -82.65) * mm});
            skLineSegment(sketch, "E291", {"start": v(-65.56, -82.65) * mm, "end": v(-65.56, -70.32) * mm});
            skLineSegment(sketch, "E292", {"start": v(-60.8, -70.32) * mm, "end": v(-65.56, -70.32) * mm});
            skLineSegment(sketch, "E293", {"start": v(-60.8, -70.32) * mm, "end": v(-60.8, -57.98) * mm});
            skLineSegment(sketch, "E294", {"start": v(-60.8, -57.98) * mm, "end": v(-65.56, -57.98) * mm});
            skLineSegment(sketch, "E295", {"start": v(-65.56, -57.98) * mm, "end": v(-65.56, -45.64) * mm});
            skLineSegment(sketch, "E296", {"start": v(-60.8, -45.64) * mm, "end": v(-65.56, -45.64) * mm});
            skLineSegment(sketch, "E297", {"start": v(-60.8, -45.64) * mm, "end": v(-60.8, -33.3) * mm});
            skLineSegment(sketch, "E298", {"start": v(-60.8, -33.3) * mm, "end": v(-65.56, -33.3) * mm});
            skLineSegment(sketch, "E299", {"start": v(-65.56, -33.3) * mm, "end": v(-65.56, -20.97) * mm});
            skLineSegment(sketch, "E300", {"start": v(-60.8, -20.97) * mm, "end": v(-65.56, -20.97) * mm});
            skLineSegment(sketch, "E301", {"start": v(-60.8, -20.97) * mm, "end": v(-60.8, -8.63) * mm});
            skLineSegment(sketch, "E302", {"start": v(-60.8, -8.63) * mm, "end": v(-65.56, -8.63) * mm});
            skLineSegment(sketch, "E303", {"start": v(-65.56, -8.63) * mm, "end": v(-65.56, 3.7) * mm});
            skLineSegment(sketch, "E304", {"start": v(-60.8, 3.7) * mm, "end": v(-65.56, 3.7) * mm});
            skLineSegment(sketch, "E305", {"start": v(-60.8, 3.7) * mm, "end": v(-60.8, 16.04) * mm});
            skLineSegment(sketch, "E306", {"start": v(-60.8, 16.04) * mm, "end": v(-65.56, 16.04) * mm});
            skLineSegment(sketch, "E307", {"start": v(-65.56, 16.04) * mm, "end": v(-65.56, 28.38) * mm});
            skLineSegment(sketch, "E308", {"start": v(-60.8, 28.38) * mm, "end": v(-65.56, 28.38) * mm});
            skLineSegment(sketch, "E309", {"start": v(-60.8, 28.38) * mm, "end": v(-60.8, 40.72) * mm});
            skLineSegment(sketch, "E310", {"start": v(-60.8, 40.72) * mm, "end": v(-65.56, 40.72) * mm});
            skLineSegment(sketch, "E311", {"start": v(-65.56, 40.72) * mm, "end": v(-65.56, 53.06) * mm});
            skLineSegment(sketch, "E312", {"start": v(-60.8, 53.06) * mm, "end": v(-65.56, 53.06) * mm});
            skLineSegment(sketch, "E313", {"start": v(-60.8, 53.06) * mm, "end": v(-60.8, 65.39) * mm});
            skLineSegment(sketch, "E314", {"start": v(-60.8, 65.39) * mm, "end": v(-65.56, 65.39) * mm});
            skLineSegment(sketch, "E315", {"start": v(-65.56, 65.39) * mm, "end": v(-65.56, 77.73) * mm});
            skLineSegment(sketch, "E316", {"start": v(-60.8, 77.73) * mm, "end": v(-65.56, 77.73) * mm});
            skLineSegment(sketch, "E317", {"start": v(-60.8, 77.73) * mm, "end": v(-60.8, 90.07) * mm});
            skLineSegment(sketch, "E318", {"start": v(-60.8, 90.07) * mm, "end": v(-65.56, 90.07) * mm});
            skLineSegment(sketch, "E319", {"start": v(-65.56, 90.07) * mm, "end": v(-65.56, 102.4) * mm});
            skLineSegment(sketch, "E320", {"start": v(-60.8, 102.4) * mm, "end": v(-65.56, 102.4) * mm});
            skLineSegment(sketch, "E321", {"start": v(-60.8, 102.4) * mm, "end": v(-60.8, 114.74) * mm});
            skLineSegment(sketch, "E322", {"start": v(-60.8, 114.74) * mm, "end": v(-65.56, 114.74) * mm});
            skLineSegment(sketch, "E323", {"start": v(-65.56, 114.74) * mm, "end": v(-65.56, 127.08) * mm});
            skLineSegment(sketch, "E324", {"start": v(-60.8, 127.08) * mm, "end": v(-65.56, 127.08) * mm});
            skLineSegment(sketch, "E325", {"start": v(-60.8, 127.08) * mm, "end": v(-60.8, 139.42) * mm});
            skLineSegment(sketch, "E326", {"start": v(-60.8, 139.42) * mm, "end": v(-65.56, 139.42) * mm});
            skLineSegment(sketch, "E327", {"start": v(-65.56, 139.42) * mm, "end": v(-65.56, 151.75) * mm});
            skLineSegment(sketch, "E328", {"start": v(-60.8, 151.75) * mm, "end": v(-65.56, 151.75) * mm});
            skLineSegment(sketch, "E329", {"start": v(-60.8, 151.75) * mm, "end": v(-60.8, 164.1) * mm});
            skLineSegment(sketch, "E330", {"start": v(-60.8, 164.1) * mm, "end": v(-65.56, 164.1) * mm});
            skLineSegment(sketch, "E331", {"start": v(-65.56, 164.1) * mm, "end": v(-65.56, 176.43) * mm});
            skLineSegment(sketch, "E332", {"start": v(-60.8, 176.43) * mm, "end": v(-65.56, 176.43) * mm});
            skLineSegment(sketch, "E333", {"start": v(-60.8, 176.43) * mm, "end": v(-60.8, 188.76) * mm});
            skLineSegment(sketch, "E334", {"start": v(-60.8, 188.76) * mm, "end": v(-65.56, 188.76) * mm});
            skLineSegment(sketch, "E335", {"start": v(-65.56, 188.76) * mm, "end": v(-65.56, 201.1) * mm});
            skLineSegment(sketch, "E336", {"start": v(-60.8, 201.1) * mm, "end": v(-65.56, 201.1) * mm});
            skLineSegment(sketch, "E337", {"start": v(-60.8, 201.1) * mm, "end": v(-60.8, 213.44) * mm});
            skLineSegment(sketch, "E338", {"start": v(-60.8, 213.44) * mm, "end": v(-65.56, 213.44) * mm});
            skLineSegment(sketch, "E339", {"start": v(-65.56, 213.44) * mm, "end": v(-65.56, 225.78) * mm});
            skLineSegment(sketch, "E340", {"start": v(-60.8, 225.78) * mm, "end": v(-65.56, 225.78) * mm});
            skLineSegment(sketch, "E341", {"start": v(-60.8, 225.78) * mm, "end": v(-60.8, 238.11) * mm});
            skLineSegment(sketch, "E342", {"start": v(-60.8, 238.11) * mm, "end": v(-65.56, 238.11) * mm});
            skLineSegment(sketch, "E343", {"start": v(-65.56, 238.11) * mm, "end": v(-65.56, 250.45) * mm});
            skLineSegment(sketch, "E344", {"start": v(-60.8, 250.45) * mm, "end": v(-65.56, 250.45) * mm});
            skLineSegment(sketch, "E345", {"start": v(-60.8, 250.45) * mm, "end": v(-60.8, 262.79) * mm});
            skLineSegment(sketch, "E346", {"start": v(-60.8, 262.79) * mm, "end": v(-65.56, 262.79) * mm});
            skLineSegment(sketch, "E347", {"start": v(-65.56, 262.79) * mm, "end": v(-65.56, 275.12) * mm});
            skLineSegment(sketch, "E348", {"start": v(-60.8, 275.12) * mm, "end": v(-65.56, 275.12) * mm});
            skLineSegment(sketch, "E349", {"start": v(-60.8, 275.12) * mm, "end": v(-60.8, 287.46) * mm});
            skLineSegment(sketch, "E350", {"start": v(-60.8, 287.46) * mm, "end": v(-65.56, 287.46) * mm});
            skLineSegment(sketch, "E351", {"start": v(-65.56, 287.46) * mm, "end": v(-65.56, 299.8) * mm});
            skLineSegment(sketch, "E352", {"start": v(-46.04, -127.24) * mm, "end": v(-39.51, -127.24) * mm});
            skLineSegment(sketch, "E353", {"start": v(-39.51, -127.24) * mm, "end": v(-39.51, -132) * mm});
            skLineSegment(sketch, "E354", {"start": v(-39.51, -132) * mm, "end": v(-28.22, -132) * mm});
            skLineSegment(sketch, "E355", {"start": v(-28.22, -127.24) * mm, "end": v(-28.22, -132) * mm});
            skLineSegment(sketch, "E356", {"start": v(-28.22, -127.24) * mm, "end": v(-16.93, -127.24) * mm});
            skLineSegment(sketch, "E357", {"start": v(-16.93, -127.24) * mm, "end": v(-16.93, -132) * mm});
            skLineSegment(sketch, "E358", {"start": v(-16.93, -132) * mm, "end": v(-5.65, -132) * mm});
            skLineSegment(sketch, "E359", {"start": v(-5.65, -127.24) * mm, "end": v(-5.65, -132) * mm});
            skLineSegment(sketch, "E360", {"start": v(-5.65, -127.24) * mm, "end": v(5.64, -127.24) * mm});
            skLineSegment(sketch, "E361", {"start": v(5.64, -127.24) * mm, "end": v(5.64, -132) * mm});
            skLineSegment(sketch, "E362", {"start": v(5.64, -132) * mm, "end": v(16.93, -132) * mm});
            skLineSegment(sketch, "E363", {"start": v(16.93, -127.24) * mm, "end": v(16.93, -132) * mm});
            skLineSegment(sketch, "E364", {"start": v(16.93, -127.24) * mm, "end": v(28.22, -127.24) * mm});
            skLineSegment(sketch, "E365", {"start": v(28.22, -127.24) * mm, "end": v(28.22, -132) * mm});
            skLineSegment(sketch, "E366", {"start": v(28.22, -132) * mm, "end": v(39.51, -132) * mm});
            skLineSegment(sketch, "E367", {"start": v(39.51, -127.24) * mm, "end": v(39.51, -132) * mm});
            skLineSegment(sketch, "E368", {"start": v(39.51, -127.24) * mm, "end": v(46.04, -127.24) * mm});
            skLineSegment(sketch, "E369", {"start": v(-46.04, -9.76) * mm, "end": v(-39.51, -9.76) * mm});
            skLineSegment(sketch, "E370", {"start": v(-39.51, -5) * mm, "end": v(-39.51, -9.76) * mm});
            skLineSegment(sketch, "E371", {"start": v(-39.51, -5) * mm, "end": v(-28.22, -5) * mm});
            skLineSegment(sketch, "E372", {"start": v(-28.22, -5) * mm, "end": v(-28.22, -9.76) * mm});
            skLineSegment(sketch, "E373", {"start": v(-28.22, -9.76) * mm, "end": v(-16.93, -9.76) * mm});
            skLineSegment(sketch, "E374", {"start": v(-16.93, -5) * mm, "end": v(-16.93, -9.76) * mm});
            skLineSegment(sketch, "E375", {"start": v(-16.93, -5) * mm, "end": v(-5.65, -5) * mm});
            skLineSegment(sketch, "E376", {"start": v(-5.65, -5) * mm, "end": v(-5.65, -9.76) * mm});
            skLineSegment(sketch, "E377", {"start": v(-5.65, -9.76) * mm, "end": v(5.64, -9.76) * mm});
            skLineSegment(sketch, "E378", {"start": v(5.64, -5) * mm, "end": v(5.64, -9.76) * mm});
            skLineSegment(sketch, "E379", {"start": v(5.64, -5) * mm, "end": v(16.93, -5) * mm});
            skLineSegment(sketch, "E380", {"start": v(16.93, -5) * mm, "end": v(16.93, -9.76) * mm});
            skLineSegment(sketch, "E381", {"start": v(16.93, -9.76) * mm, "end": v(28.22, -9.76) * mm});
            skLineSegment(sketch, "E382", {"start": v(28.22, -5) * mm, "end": v(28.22, -9.76) * mm});
            skLineSegment(sketch, "E383", {"start": v(28.22, -5) * mm, "end": v(39.51, -5) * mm});
            skLineSegment(sketch, "E384", {"start": v(39.51, -5) * mm, "end": v(39.51, -9.76) * mm});
            skLineSegment(sketch, "E385", {"start": v(39.51, -9.76) * mm, "end": v(46.04, -9.76) * mm});
            skLineSegment(sketch, "E386", {"start": v(-46.04, -127.24) * mm, "end": v(-46.04, -120.46) * mm});
            skLineSegment(sketch, "E387", {"start": v(-46.04, -120.46) * mm, "end": v(-50.8, -120.46) * mm});
            skLineSegment(sketch, "E388", {"start": v(-50.8, -120.46) * mm, "end": v(-50.8, -108.91) * mm});
            skLineSegment(sketch, "E389", {"start": v(-46.04, -108.91) * mm, "end": v(-50.8, -108.91) * mm});
            skLineSegment(sketch, "E390", {"start": v(-46.04, -108.91) * mm, "end": v(-46.04, -97.36) * mm});
            skLineSegment(sketch, "E391", {"start": v(-46.04, -97.36) * mm, "end": v(-50.8, -97.36) * mm});
            skLineSegment(sketch, "E392", {"start": v(-50.8, -97.36) * mm, "end": v(-50.8, -85.82) * mm});
            skLineSegment(sketch, "E393", {"start": v(-46.04, -85.82) * mm, "end": v(-50.8, -85.82) * mm});
            skLineSegment(sketch, "E394", {"start": v(-46.04, -85.82) * mm, "end": v(-46.04, -74.27) * mm});
            skLineSegment(sketch, "E395", {"start": v(-46.04, -74.27) * mm, "end": v(-50.8, -74.27) * mm});
            skLineSegment(sketch, "E396", {"start": v(-50.8, -74.27) * mm, "end": v(-50.8, -62.73) * mm});
            skLineSegment(sketch, "E397", {"start": v(-46.04, -62.73) * mm, "end": v(-50.8, -62.73) * mm});
            skLineSegment(sketch, "E398", {"start": v(-46.04, -62.73) * mm, "end": v(-46.04, -51.18) * mm});
            skLineSegment(sketch, "E399", {"start": v(-46.04, -51.18) * mm, "end": v(-50.8, -51.18) * mm});
            skLineSegment(sketch, "E400", {"start": v(-50.8, -51.18) * mm, "end": v(-50.8, -39.64) * mm});
            skLineSegment(sketch, "E401", {"start": v(-46.04, -39.64) * mm, "end": v(-50.8, -39.64) * mm});
            skLineSegment(sketch, "E402", {"start": v(-46.04, -39.64) * mm, "end": v(-46.04, -28.1) * mm});
            skLineSegment(sketch, "E403", {"start": v(-46.04, -28.1) * mm, "end": v(-50.8, -28.1) * mm});
            skLineSegment(sketch, "E404", {"start": v(-50.8, -28.1) * mm, "end": v(-50.8, -16.55) * mm});
            skLineSegment(sketch, "E405", {"start": v(-46.04, -16.55) * mm, "end": v(-50.8, -16.55) * mm});
            skLineSegment(sketch, "E406", {"start": v(-46.04, -16.55) * mm, "end": v(-46.04, -9.76) * mm});
            skLineSegment(sketch, "E407", {"start": v(46.04, -127.24) * mm, "end": v(46.04, -120.46) * mm});
            skLineSegment(sketch, "E408", {"start": v(50.8, -120.46) * mm, "end": v(46.04, -120.46) * mm});
            skLineSegment(sketch, "E409", {"start": v(50.8, -120.46) * mm, "end": v(50.8, -108.91) * mm});
            skLineSegment(sketch, "E410", {"start": v(50.8, -108.91) * mm, "end": v(46.04, -108.91) * mm});
            skLineSegment(sketch, "E411", {"start": v(46.04, -108.91) * mm, "end": v(46.04, -97.36) * mm});
            skLineSegment(sketch, "E412", {"start": v(50.8, -97.36) * mm, "end": v(46.04, -97.36) * mm});
            skLineSegment(sketch, "E413", {"start": v(50.8, -97.36) * mm, "end": v(50.8, -85.82) * mm});
            skLineSegment(sketch, "E414", {"start": v(50.8, -85.82) * mm, "end": v(46.04, -85.82) * mm});
            skLineSegment(sketch, "E415", {"start": v(46.04, -85.82) * mm, "end": v(46.04, -74.27) * mm});
            skLineSegment(sketch, "E416", {"start": v(50.8, -74.27) * mm, "end": v(46.04, -74.27) * mm});
            skLineSegment(sketch, "E417", {"start": v(50.8, -74.27) * mm, "end": v(50.8, -62.73) * mm});
            skLineSegment(sketch, "E418", {"start": v(50.8, -62.73) * mm, "end": v(46.04, -62.73) * mm});
            skLineSegment(sketch, "E419", {"start": v(46.04, -62.73) * mm, "end": v(46.04, -51.18) * mm});
            skLineSegment(sketch, "E420", {"start": v(50.8, -51.18) * mm, "end": v(46.04, -51.18) * mm});
            skLineSegment(sketch, "E421", {"start": v(50.8, -51.18) * mm, "end": v(50.8, -39.64) * mm});
            skLineSegment(sketch, "E422", {"start": v(50.8, -39.64) * mm, "end": v(46.04, -39.64) * mm});
            skLineSegment(sketch, "E423", {"start": v(46.04, -39.64) * mm, "end": v(46.04, -28.1) * mm});
            skLineSegment(sketch, "E424", {"start": v(50.8, -28.1) * mm, "end": v(46.04, -28.1) * mm});
            skLineSegment(sketch, "E425", {"start": v(50.8, -28.1) * mm, "end": v(50.8, -16.55) * mm});
            skLineSegment(sketch, "E426", {"start": v(50.8, -16.55) * mm, "end": v(46.04, -16.55) * mm});
            skLineSegment(sketch, "E427", {"start": v(46.04, -16.55) * mm, "end": v(46.04, -9.76) * mm});
            skLineSegment(sketch, "E428", {"start": v(60.8, -132) * mm, "end": v(72.34, -132) * mm});
            skLineSegment(sketch, "E429", {"start": v(72.34, -127.24) * mm, "end": v(72.34, -132) * mm});
            skLineSegment(sketch, "E430", {"start": v(72.34, -127.24) * mm, "end": v(83.9, -127.24) * mm});
            skLineSegment(sketch, "E431", {"start": v(83.9, -127.24) * mm, "end": v(83.9, -132) * mm});
            skLineSegment(sketch, "E432", {"start": v(83.9, -132) * mm, "end": v(95.44, -132) * mm});
            skLineSegment(sketch, "E433", {"start": v(95.44, -127.24) * mm, "end": v(95.44, -132) * mm});
            skLineSegment(sketch, "E434", {"start": v(95.44, -127.24) * mm, "end": v(106.98, -127.24) * mm});
            skLineSegment(sketch, "E435", {"start": v(106.98, -127.24) * mm, "end": v(106.98, -132) * mm});
            skLineSegment(sketch, "E436", {"start": v(106.98, -132) * mm, "end": v(118.53, -132) * mm});
            skLineSegment(sketch, "E437", {"start": v(118.53, -127.24) * mm, "end": v(118.53, -132) * mm});
            skLineSegment(sketch, "E438", {"start": v(118.53, -127.24) * mm, "end": v(130.07, -127.24) * mm});
            skLineSegment(sketch, "E439", {"start": v(130.07, -127.24) * mm, "end": v(130.07, -132) * mm});
            skLineSegment(sketch, "E440", {"start": v(130.07, -132) * mm, "end": v(141.62, -132) * mm});
            skLineSegment(sketch, "E441", {"start": v(141.62, -127.24) * mm, "end": v(141.62, -132) * mm});
            skLineSegment(sketch, "E442", {"start": v(141.62, -127.24) * mm, "end": v(153.16, -127.24) * mm});
            skLineSegment(sketch, "E443", {"start": v(153.16, -127.24) * mm, "end": v(153.16, -132) * mm});
            skLineSegment(sketch, "E444", {"start": v(153.16, -132) * mm, "end": v(164.71, -132) * mm});
            skLineSegment(sketch, "E445", {"start": v(164.71, -127.24) * mm, "end": v(164.71, -132) * mm});
            skLineSegment(sketch, "E446", {"start": v(164.71, -127.24) * mm, "end": v(176.25, -127.24) * mm});
            skLineSegment(sketch, "E447", {"start": v(176.25, -127.24) * mm, "end": v(176.25, -132) * mm});
            skLineSegment(sketch, "E448", {"start": v(176.25, -132) * mm, "end": v(183.04, -132) * mm});
            skLineSegment(sketch, "E449", {"start": v(60.8, 299.8) * mm, "end": v(72.34, 299.8) * mm});
            skLineSegment(sketch, "E450", {"start": v(72.34, 299.8) * mm, "end": v(72.34, 295.04) * mm});
            skLineSegment(sketch, "E451", {"start": v(72.34, 295.04) * mm, "end": v(83.9, 295.04) * mm});
            skLineSegment(sketch, "E452", {"start": v(83.9, 299.8) * mm, "end": v(83.9, 295.04) * mm});
            skLineSegment(sketch, "E453", {"start": v(83.9, 299.8) * mm, "end": v(95.44, 299.8) * mm});
            skLineSegment(sketch, "E454", {"start": v(95.44, 299.8) * mm, "end": v(95.44, 295.04) * mm});
            skLineSegment(sketch, "E455", {"start": v(95.44, 295.04) * mm, "end": v(106.98, 295.04) * mm});
            skLineSegment(sketch, "E456", {"start": v(106.98, 299.8) * mm, "end": v(106.98, 295.04) * mm});
            skLineSegment(sketch, "E457", {"start": v(106.98, 299.8) * mm, "end": v(118.53, 299.8) * mm});
            skLineSegment(sketch, "E458", {"start": v(118.53, 299.8) * mm, "end": v(118.53, 295.04) * mm});
            skLineSegment(sketch, "E459", {"start": v(118.53, 295.04) * mm, "end": v(130.07, 295.04) * mm});
            skLineSegment(sketch, "E460", {"start": v(130.07, 299.8) * mm, "end": v(130.07, 295.04) * mm});
            skLineSegment(sketch, "E461", {"start": v(130.07, 299.8) * mm, "end": v(141.62, 299.8) * mm});
            skLineSegment(sketch, "E462", {"start": v(141.62, 299.8) * mm, "end": v(141.62, 295.04) * mm});
            skLineSegment(sketch, "E463", {"start": v(141.62, 295.04) * mm, "end": v(153.16, 295.04) * mm});
            skLineSegment(sketch, "E464", {"start": v(153.16, 299.8) * mm, "end": v(153.16, 295.04) * mm});
            skLineSegment(sketch, "E465", {"start": v(153.16, 299.8) * mm, "end": v(164.71, 299.8) * mm});
            skLineSegment(sketch, "E466", {"start": v(164.71, 299.8) * mm, "end": v(164.71, 295.04) * mm});
            skLineSegment(sketch, "E467", {"start": v(164.71, 295.04) * mm, "end": v(176.25, 295.04) * mm});
            skLineSegment(sketch, "E468", {"start": v(176.25, 299.8) * mm, "end": v(176.25, 295.04) * mm});
            skLineSegment(sketch, "E469", {"start": v(176.25, 299.8) * mm, "end": v(183.04, 299.8) * mm});
            skLineSegment(sketch, "E470", {"start": v(60.8, -132) * mm, "end": v(60.8, -119.66) * mm});
            skLineSegment(sketch, "E471", {"start": v(65.56, -119.66) * mm, "end": v(60.8, -119.66) * mm});
            skLineSegment(sketch, "E472", {"start": v(65.56, -119.66) * mm, "end": v(65.56, -107.33) * mm});
            skLineSegment(sketch, "E473", {"start": v(65.56, -107.33) * mm, "end": v(60.8, -107.33) * mm});
            skLineSegment(sketch, "E474", {"start": v(60.8, -107.33) * mm, "end": v(60.8, -94.99) * mm});
            skLineSegment(sketch, "E475", {"start": v(65.56, -94.99) * mm, "end": v(60.8, -94.99) * mm});
            skLineSegment(sketch, "E476", {"start": v(65.56, -94.99) * mm, "end": v(65.56, -82.65) * mm});
            skLineSegment(sketch, "E477", {"start": v(65.56, -82.65) * mm, "end": v(60.8, -82.65) * mm});
            skLineSegment(sketch, "E478", {"start": v(60.8, -82.65) * mm, "end": v(60.8, -70.32) * mm});
            skLineSegment(sketch, "E479", {"start": v(65.56, -70.32) * mm, "end": v(60.8, -70.32) * mm});
            skLineSegment(sketch, "E480", {"start": v(65.56, -70.32) * mm, "end": v(65.56, -57.98) * mm});
            skLineSegment(sketch, "E481", {"start": v(65.56, -57.98) * mm, "end": v(60.8, -57.98) * mm});
            skLineSegment(sketch, "E482", {"start": v(60.8, -57.98) * mm, "end": v(60.8, -45.64) * mm});
            skLineSegment(sketch, "E483", {"start": v(65.56, -45.64) * mm, "end": v(60.8, -45.64) * mm});
            skLineSegment(sketch, "E484", {"start": v(65.56, -45.64) * mm, "end": v(65.56, -33.3) * mm});
            skLineSegment(sketch, "E485", {"start": v(65.56, -33.3) * mm, "end": v(60.8, -33.3) * mm});
            skLineSegment(sketch, "E486", {"start": v(60.8, -33.3) * mm, "end": v(60.8, -20.97) * mm});
            skLineSegment(sketch, "E487", {"start": v(65.56, -20.97) * mm, "end": v(60.8, -20.97) * mm});
            skLineSegment(sketch, "E488", {"start": v(65.56, -20.97) * mm, "end": v(65.56, -8.63) * mm});
            skLineSegment(sketch, "E489", {"start": v(65.56, -8.63) * mm, "end": v(60.8, -8.63) * mm});
            skLineSegment(sketch, "E490", {"start": v(60.8, -8.63) * mm, "end": v(60.8, 3.7) * mm});
            skLineSegment(sketch, "E491", {"start": v(65.56, 3.7) * mm, "end": v(60.8, 3.7) * mm});
            skLineSegment(sketch, "E492", {"start": v(65.56, 3.7) * mm, "end": v(65.56, 16.04) * mm});
            skLineSegment(sketch, "E493", {"start": v(65.56, 16.04) * mm, "end": v(60.8, 16.04) * mm});
            skLineSegment(sketch, "E494", {"start": v(60.8, 16.04) * mm, "end": v(60.8, 28.38) * mm});
            skLineSegment(sketch, "E495", {"start": v(65.56, 28.38) * mm, "end": v(60.8, 28.38) * mm});
            skLineSegment(sketch, "E496", {"start": v(65.56, 28.38) * mm, "end": v(65.56, 40.72) * mm});
            skLineSegment(sketch, "E497", {"start": v(65.56, 40.72) * mm, "end": v(60.8, 40.72) * mm});
            skLineSegment(sketch, "E498", {"start": v(60.8, 40.72) * mm, "end": v(60.8, 53.06) * mm});
            skLineSegment(sketch, "E499", {"start": v(65.56, 53.06) * mm, "end": v(60.8, 53.06) * mm});
            skLineSegment(sketch, "E500", {"start": v(65.56, 53.06) * mm, "end": v(65.56, 65.39) * mm});
            skLineSegment(sketch, "E501", {"start": v(65.56, 65.39) * mm, "end": v(60.8, 65.39) * mm});
            skLineSegment(sketch, "E502", {"start": v(60.8, 65.39) * mm, "end": v(60.8, 77.73) * mm});
            skLineSegment(sketch, "E503", {"start": v(65.56, 77.73) * mm, "end": v(60.8, 77.73) * mm});
            skLineSegment(sketch, "E504", {"start": v(65.56, 77.73) * mm, "end": v(65.56, 90.07) * mm});
            skLineSegment(sketch, "E505", {"start": v(60.8, 90.07) * mm, "end": v(60.8, 102.4) * mm});
            skLineSegment(sketch, "E506", {"start": v(65.56, 102.4) * mm, "end": v(60.8, 102.4) * mm});
            skLineSegment(sketch, "E507", {"start": v(65.56, 102.4) * mm, "end": v(65.56, 114.74) * mm});
            skLineSegment(sketch, "E508", {"start": v(65.56, 114.74) * mm, "end": v(60.8, 114.74) * mm});
            skLineSegment(sketch, "E509", {"start": v(60.8, 114.74) * mm, "end": v(60.8, 127.08) * mm});
            skLineSegment(sketch, "E510", {"start": v(65.56, 127.08) * mm, "end": v(60.8, 127.08) * mm});
            skLineSegment(sketch, "E511", {"start": v(65.56, 127.08) * mm, "end": v(65.56, 139.42) * mm});
            skLineSegment(sketch, "E512", {"start": v(65.56, 139.42) * mm, "end": v(60.8, 139.42) * mm});
            skLineSegment(sketch, "E513", {"start": v(60.8, 139.42) * mm, "end": v(60.8, 151.75) * mm});
            skLineSegment(sketch, "E514", {"start": v(65.56, 151.75) * mm, "end": v(60.8, 151.75) * mm});
            skLineSegment(sketch, "E515", {"start": v(65.56, 151.75) * mm, "end": v(65.56, 164.1) * mm});
            skLineSegment(sketch, "E516", {"start": v(65.56, 164.1) * mm, "end": v(60.8, 164.1) * mm});
            skLineSegment(sketch, "E517", {"start": v(60.8, 164.1) * mm, "end": v(60.8, 176.43) * mm});
            skLineSegment(sketch, "E518", {"start": v(65.56, 176.43) * mm, "end": v(60.8, 176.43) * mm});
            skLineSegment(sketch, "E519", {"start": v(65.56, 176.43) * mm, "end": v(65.56, 188.76) * mm});
            skLineSegment(sketch, "E520", {"start": v(65.56, 188.76) * mm, "end": v(60.8, 188.76) * mm});
            skLineSegment(sketch, "E521", {"start": v(60.8, 188.76) * mm, "end": v(60.8, 201.1) * mm});
            skLineSegment(sketch, "E522", {"start": v(65.56, 201.1) * mm, "end": v(60.8, 201.1) * mm});
            skLineSegment(sketch, "E523", {"start": v(65.56, 201.1) * mm, "end": v(65.56, 213.44) * mm});
            skLineSegment(sketch, "E524", {"start": v(65.56, 213.44) * mm, "end": v(60.8, 213.44) * mm});
            skLineSegment(sketch, "E525", {"start": v(60.8, 213.44) * mm, "end": v(60.8, 225.78) * mm});
            skLineSegment(sketch, "E526", {"start": v(65.56, 225.78) * mm, "end": v(60.8, 225.78) * mm});
            skLineSegment(sketch, "E527", {"start": v(65.56, 225.78) * mm, "end": v(65.56, 238.11) * mm});
            skLineSegment(sketch, "E528", {"start": v(65.56, 238.11) * mm, "end": v(60.8, 238.11) * mm});
            skLineSegment(sketch, "E529", {"start": v(60.8, 238.11) * mm, "end": v(60.8, 250.45) * mm});
            skLineSegment(sketch, "E530", {"start": v(65.56, 250.45) * mm, "end": v(60.8, 250.45) * mm});
            skLineSegment(sketch, "E531", {"start": v(65.56, 250.45) * mm, "end": v(65.56, 262.79) * mm});
            skLineSegment(sketch, "E532", {"start": v(65.56, 262.79) * mm, "end": v(60.8, 262.79) * mm});
            skLineSegment(sketch, "E533", {"start": v(60.8, 262.79) * mm, "end": v(60.8, 275.12) * mm});
            skLineSegment(sketch, "E534", {"start": v(65.56, 275.12) * mm, "end": v(60.8, 275.12) * mm});
            skLineSegment(sketch, "E535", {"start": v(65.56, 275.12) * mm, "end": v(65.56, 287.46) * mm});
            skLineSegment(sketch, "E536", {"start": v(65.56, 287.46) * mm, "end": v(60.8, 287.46) * mm});
            skLineSegment(sketch, "E537", {"start": v(60.8, 287.46) * mm, "end": v(60.8, 299.8) * mm});
            skLineSegment(sketch, "E538", {"start": v(183.04, -132) * mm, "end": v(183.04, -119.66) * mm});
            skLineSegment(sketch, "E539", {"start": v(187.8, -119.66) * mm, "end": v(183.04, -119.66) * mm});
            skLineSegment(sketch, "E540", {"start": v(187.8, -119.66) * mm, "end": v(187.8, -107.33) * mm});
            skLineSegment(sketch, "E541", {"start": v(187.8, -107.33) * mm, "end": v(183.04, -107.33) * mm});
            skLineSegment(sketch, "E542", {"start": v(183.04, -107.33) * mm, "end": v(183.04, -94.99) * mm});
            skLineSegment(sketch, "E543", {"start": v(187.8, -94.99) * mm, "end": v(183.04, -94.99) * mm});
            skLineSegment(sketch, "E544", {"start": v(187.8, -94.99) * mm, "end": v(187.8, -82.65) * mm});
            skLineSegment(sketch, "E545", {"start": v(187.8, -82.65) * mm, "end": v(183.04, -82.65) * mm});
            skLineSegment(sketch, "E546", {"start": v(183.04, -82.65) * mm, "end": v(183.04, -70.32) * mm});
            skLineSegment(sketch, "E547", {"start": v(187.8, -70.32) * mm, "end": v(183.04, -70.32) * mm});
            skLineSegment(sketch, "E548", {"start": v(187.8, -70.32) * mm, "end": v(187.8, -57.98) * mm});
            skLineSegment(sketch, "E549", {"start": v(187.8, -57.98) * mm, "end": v(183.04, -57.98) * mm});
            skLineSegment(sketch, "E550", {"start": v(183.04, -57.98) * mm, "end": v(183.04, -45.64) * mm});
            skLineSegment(sketch, "E551", {"start": v(187.8, -45.64) * mm, "end": v(183.04, -45.64) * mm});
            skLineSegment(sketch, "E552", {"start": v(187.8, -45.64) * mm, "end": v(187.8, -33.3) * mm});
            skLineSegment(sketch, "E553", {"start": v(187.8, -33.3) * mm, "end": v(183.04, -33.3) * mm});
            skLineSegment(sketch, "E554", {"start": v(183.04, -33.3) * mm, "end": v(183.04, -20.97) * mm});
            skLineSegment(sketch, "E555", {"start": v(187.8, -20.97) * mm, "end": v(183.04, -20.97) * mm});
            skLineSegment(sketch, "E556", {"start": v(187.8, -20.97) * mm, "end": v(187.8, -8.63) * mm});
            skLineSegment(sketch, "E557", {"start": v(187.8, -8.63) * mm, "end": v(183.04, -8.63) * mm});
            skLineSegment(sketch, "E558", {"start": v(183.04, -8.63) * mm, "end": v(183.04, 3.7) * mm});
            skLineSegment(sketch, "E559", {"start": v(187.8, 3.7) * mm, "end": v(183.04, 3.7) * mm});
            skLineSegment(sketch, "E560", {"start": v(187.8, 3.7) * mm, "end": v(187.8, 16.04) * mm});
            skLineSegment(sketch, "E561", {"start": v(187.8, 16.04) * mm, "end": v(183.04, 16.04) * mm});
            skLineSegment(sketch, "E562", {"start": v(183.04, 16.04) * mm, "end": v(183.04, 28.38) * mm});
            skLineSegment(sketch, "E563", {"start": v(187.8, 28.38) * mm, "end": v(183.04, 28.38) * mm});
            skLineSegment(sketch, "E564", {"start": v(187.8, 28.38) * mm, "end": v(187.8, 40.72) * mm});
            skLineSegment(sketch, "E565", {"start": v(187.8, 40.72) * mm, "end": v(183.04, 40.72) * mm});
            skLineSegment(sketch, "E566", {"start": v(183.04, 40.72) * mm, "end": v(183.04, 53.06) * mm});
            skLineSegment(sketch, "E567", {"start": v(187.8, 53.06) * mm, "end": v(183.04, 53.06) * mm});
            skLineSegment(sketch, "E568", {"start": v(187.8, 53.06) * mm, "end": v(187.8, 65.39) * mm});
            skLineSegment(sketch, "E569", {"start": v(187.8, 65.39) * mm, "end": v(183.04, 65.39) * mm});
            skLineSegment(sketch, "E570", {"start": v(183.04, 65.39) * mm, "end": v(183.04, 77.73) * mm});
            skLineSegment(sketch, "E571", {"start": v(187.8, 77.73) * mm, "end": v(183.04, 77.73) * mm});
            skLineSegment(sketch, "E572", {"start": v(187.8, 77.73) * mm, "end": v(187.8, 90.07) * mm});
            skLineSegment(sketch, "E573", {"start": v(187.8, 90.07) * mm, "end": v(183.04, 90.07) * mm});
            skLineSegment(sketch, "E574", {"start": v(183.04, 90.07) * mm, "end": v(183.04, 102.4) * mm});
            skLineSegment(sketch, "E575", {"start": v(187.8, 102.4) * mm, "end": v(183.04, 102.4) * mm});
            skLineSegment(sketch, "E576", {"start": v(187.8, 102.4) * mm, "end": v(187.8, 114.74) * mm});
            skLineSegment(sketch, "E577", {"start": v(187.8, 114.74) * mm, "end": v(183.04, 114.74) * mm});
            skLineSegment(sketch, "E578", {"start": v(183.04, 114.74) * mm, "end": v(183.04, 127.08) * mm});
            skLineSegment(sketch, "E579", {"start": v(187.8, 127.08) * mm, "end": v(183.04, 127.08) * mm});
            skLineSegment(sketch, "E580", {"start": v(187.8, 127.08) * mm, "end": v(187.8, 139.42) * mm});
            skLineSegment(sketch, "E581", {"start": v(187.8, 139.42) * mm, "end": v(183.04, 139.42) * mm});
            skLineSegment(sketch, "E582", {"start": v(183.04, 139.42) * mm, "end": v(183.04, 151.75) * mm});
            skLineSegment(sketch, "E583", {"start": v(187.8, 151.75) * mm, "end": v(183.04, 151.75) * mm});
            skLineSegment(sketch, "E584", {"start": v(187.8, 151.75) * mm, "end": v(187.8, 164.1) * mm});
            skLineSegment(sketch, "E585", {"start": v(187.8, 164.1) * mm, "end": v(183.04, 164.1) * mm});
            skLineSegment(sketch, "E586", {"start": v(183.04, 164.1) * mm, "end": v(183.04, 176.43) * mm});
            skLineSegment(sketch, "E587", {"start": v(187.8, 176.43) * mm, "end": v(183.04, 176.43) * mm});
            skLineSegment(sketch, "E588", {"start": v(187.8, 176.43) * mm, "end": v(187.8, 188.76) * mm});
            skLineSegment(sketch, "E589", {"start": v(187.8, 188.76) * mm, "end": v(183.04, 188.76) * mm});
            skLineSegment(sketch, "E590", {"start": v(183.04, 188.76) * mm, "end": v(183.04, 201.1) * mm});
            skLineSegment(sketch, "E591", {"start": v(187.8, 201.1) * mm, "end": v(183.04, 201.1) * mm});
            skLineSegment(sketch, "E592", {"start": v(187.8, 201.1) * mm, "end": v(187.8, 213.44) * mm});
            skLineSegment(sketch, "E593", {"start": v(187.8, 213.44) * mm, "end": v(183.04, 213.44) * mm});
            skLineSegment(sketch, "E594", {"start": v(183.04, 213.44) * mm, "end": v(183.04, 225.78) * mm});
            skLineSegment(sketch, "E595", {"start": v(187.8, 225.78) * mm, "end": v(183.04, 225.78) * mm});
            skLineSegment(sketch, "E596", {"start": v(187.8, 225.78) * mm, "end": v(187.8, 238.11) * mm});
            skLineSegment(sketch, "E597", {"start": v(187.8, 238.11) * mm, "end": v(183.04, 238.11) * mm});
            skLineSegment(sketch, "E598", {"start": v(183.04, 238.11) * mm, "end": v(183.04, 250.45) * mm});
            skLineSegment(sketch, "E599", {"start": v(187.8, 250.45) * mm, "end": v(183.04, 250.45) * mm});
            skLineSegment(sketch, "E600", {"start": v(187.8, 250.45) * mm, "end": v(187.8, 262.79) * mm});
            skLineSegment(sketch, "E601", {"start": v(187.8, 262.79) * mm, "end": v(183.04, 262.79) * mm});
            skLineSegment(sketch, "E602", {"start": v(183.04, 262.79) * mm, "end": v(183.04, 275.12) * mm});
            skLineSegment(sketch, "E603", {"start": v(187.8, 275.12) * mm, "end": v(183.04, 275.12) * mm});
            skLineSegment(sketch, "E604", {"start": v(187.8, 275.12) * mm, "end": v(187.8, 287.46) * mm});
            skLineSegment(sketch, "E605", {"start": v(187.8, 287.46) * mm, "end": v(183.04, 287.46) * mm});
            skLineSegment(sketch, "E606", {"start": v(183.04, 287.46) * mm, "end": v(183.04, 299.8) * mm});
            skLineSegment(sketch, "E607", {"start": v(-50.8, 5) * mm, "end": v(-39.51, 5) * mm});
            skLineSegment(sketch, "E608", {"start": v(-39.51, 9.76) * mm, "end": v(-39.51, 5) * mm});
            skLineSegment(sketch, "E609", {"start": v(-39.51, 9.76) * mm, "end": v(-28.22, 9.76) * mm});
            skLineSegment(sketch, "E610", {"start": v(-28.22, 9.76) * mm, "end": v(-28.22, 5) * mm});
            skLineSegment(sketch, "E611", {"start": v(-28.22, 5) * mm, "end": v(-16.93, 5) * mm});
            skLineSegment(sketch, "E612", {"start": v(-16.93, 9.76) * mm, "end": v(-16.93, 5) * mm});
            skLineSegment(sketch, "E613", {"start": v(-16.93, 9.76) * mm, "end": v(-5.65, 9.76) * mm});
            skLineSegment(sketch, "E614", {"start": v(-5.65, 9.76) * mm, "end": v(-5.65, 5) * mm});
            skLineSegment(sketch, "E615", {"start": v(-5.65, -40.07) * mm, "end": v(5.64, -40.07) * mm});
            skLineSegment(sketch, "E616", {"start": v(5.64, 9.76) * mm, "end": v(5.64, 5) * mm});
            skLineSegment(sketch, "E617", {"start": v(5.64, 9.76) * mm, "end": v(16.93, 9.76) * mm});
            skLineSegment(sketch, "E618", {"start": v(16.93, 9.76) * mm, "end": v(16.93, 5) * mm});
            skLineSegment(sketch, "E619", {"start": v(16.93, 5) * mm, "end": v(28.22, 5) * mm});
            skLineSegment(sketch, "E620", {"start": v(28.22, 9.76) * mm, "end": v(28.22, 5) * mm});
            skLineSegment(sketch, "E621", {"start": v(28.22, 9.76) * mm, "end": v(39.51, 9.76) * mm});
            skLineSegment(sketch, "E622", {"start": v(39.51, 9.76) * mm, "end": v(39.51, 5) * mm});
            skLineSegment(sketch, "E623", {"start": v(39.51, 5) * mm, "end": v(46.04, 5) * mm});
            skLineSegment(sketch, "E624", {"start": v(-50.8, 436.8) * mm, "end": v(-39.51, 436.8) * mm});
            skLineSegment(sketch, "E625", {"start": v(-39.51, 436.8) * mm, "end": v(-39.51, 432.04) * mm});
            skLineSegment(sketch, "E626", {"start": v(-39.51, 432.04) * mm, "end": v(-28.22, 432.04) * mm});
            skLineSegment(sketch, "E627", {"start": v(-28.22, 436.8) * mm, "end": v(-28.22, 432.04) * mm});
            skLineSegment(sketch, "E628", {"start": v(-28.22, 436.8) * mm, "end": v(-16.93, 436.8) * mm});
            skLineSegment(sketch, "E629", {"start": v(-16.93, 436.8) * mm, "end": v(-16.93, 432.04) * mm});
            skLineSegment(sketch, "E630", {"start": v(-16.93, 432.04) * mm, "end": v(-5.65, 432.04) * mm});
            skLineSegment(sketch, "E631", {"start": v(-5.65, 436.8) * mm, "end": v(-5.65, 432.04) * mm});
            skLineSegment(sketch, "E632", {"start": v(-5.65, 391.73) * mm, "end": v(5.64, 391.73) * mm});
            skLineSegment(sketch, "E633", {"start": v(5.64, 436.8) * mm, "end": v(5.64, 432.04) * mm});
            skLineSegment(sketch, "E634", {"start": v(5.64, 432.04) * mm, "end": v(16.93, 432.04) * mm});
            skLineSegment(sketch, "E635", {"start": v(16.93, 436.8) * mm, "end": v(16.93, 432.04) * mm});
            skLineSegment(sketch, "E636", {"start": v(16.93, 436.8) * mm, "end": v(28.22, 436.8) * mm});
            skLineSegment(sketch, "E637", {"start": v(28.22, 436.8) * mm, "end": v(28.22, 432.04) * mm});
            skLineSegment(sketch, "E638", {"start": v(28.22, 432.04) * mm, "end": v(39.51, 432.04) * mm});
            skLineSegment(sketch, "E639", {"start": v(39.51, 436.8) * mm, "end": v(39.51, 432.04) * mm});
            skLineSegment(sketch, "E640", {"start": v(39.51, 436.8) * mm, "end": v(46.04, 436.8) * mm});
            skLineSegment(sketch, "E641", {"start": v(-50.8, 5) * mm, "end": v(-50.8, 17.34) * mm});
            skLineSegment(sketch, "E642", {"start": v(-46.04, 17.34) * mm, "end": v(-50.8, 17.34) * mm});
            skLineSegment(sketch, "E643", {"start": v(-46.04, 17.34) * mm, "end": v(-46.04, 29.67) * mm});
            skLineSegment(sketch, "E644", {"start": v(-46.04, 29.67) * mm, "end": v(-50.8, 29.67) * mm});
            skLineSegment(sketch, "E645", {"start": v(-50.8, 29.67) * mm, "end": v(-50.8, 42) * mm});
            skLineSegment(sketch, "E646", {"start": v(-46.04, 42) * mm, "end": v(-50.8, 42) * mm});
            skLineSegment(sketch, "E647", {"start": v(-46.04, 42) * mm, "end": v(-46.04, 54.35) * mm});
            skLineSegment(sketch, "E648", {"start": v(-46.04, 54.35) * mm, "end": v(-50.8, 54.35) * mm});
            skLineSegment(sketch, "E649", {"start": v(-50.8, 54.35) * mm, "end": v(-50.8, 66.68) * mm});
            skLineSegment(sketch, "E650", {"start": v(-46.04, 66.68) * mm, "end": v(-50.8, 66.68) * mm});
            skLineSegment(sketch, "E651", {"start": v(-46.04, 66.68) * mm, "end": v(-46.04, 79.02) * mm});
            skLineSegment(sketch, "E652", {"start": v(-46.04, 79.02) * mm, "end": v(-50.8, 79.02) * mm});
            skLineSegment(sketch, "E653", {"start": v(-50.8, 79.02) * mm, "end": v(-50.8, 91.36) * mm});
            skLineSegment(sketch, "E654", {"start": v(-46.04, 91.36) * mm, "end": v(-50.8, 91.36) * mm});
            skLineSegment(sketch, "E655", {"start": v(-46.04, 91.36) * mm, "end": v(-46.04, 103.7) * mm});
            skLineSegment(sketch, "E656", {"start": v(-46.04, 103.7) * mm, "end": v(-50.8, 103.7) * mm});
            skLineSegment(sketch, "E657", {"start": v(-50.8, 103.7) * mm, "end": v(-50.8, 116.03) * mm});
            skLineSegment(sketch, "E658", {"start": v(-46.04, 116.03) * mm, "end": v(-50.8, 116.03) * mm});
            skLineSegment(sketch, "E659", {"start": v(-46.04, 116.03) * mm, "end": v(-46.04, 128.37) * mm});
            skLineSegment(sketch, "E660", {"start": v(-46.04, 128.37) * mm, "end": v(-50.8, 128.37) * mm});
            skLineSegment(sketch, "E661", {"start": v(-50.8, 128.37) * mm, "end": v(-50.8, 140.7) * mm});
            skLineSegment(sketch, "E662", {"start": v(-46.04, 140.7) * mm, "end": v(-50.8, 140.7) * mm});
            skLineSegment(sketch, "E663", {"start": v(-46.04, 140.7) * mm, "end": v(-46.04, 153.04) * mm});
            skLineSegment(sketch, "E664", {"start": v(-46.04, 153.04) * mm, "end": v(-50.8, 153.04) * mm});
            skLineSegment(sketch, "E665", {"start": v(-50.8, 153.04) * mm, "end": v(-50.8, 165.38) * mm});
            skLineSegment(sketch, "E666", {"start": v(-46.04, 165.38) * mm, "end": v(-50.8, 165.38) * mm});
            skLineSegment(sketch, "E667", {"start": v(-46.04, 165.38) * mm, "end": v(-46.04, 177.72) * mm});
            skLineSegment(sketch, "E668", {"start": v(-46.04, 177.72) * mm, "end": v(-50.8, 177.72) * mm});
            skLineSegment(sketch, "E669", {"start": v(-50.8, 177.72) * mm, "end": v(-50.8, 190.06) * mm});
            skLineSegment(sketch, "E670", {"start": v(-46.04, 190.06) * mm, "end": v(-50.8, 190.06) * mm});
            skLineSegment(sketch, "E671", {"start": v(-46.04, 190.06) * mm, "end": v(-46.04, 202.4) * mm});
            skLineSegment(sketch, "E672", {"start": v(-46.04, 202.4) * mm, "end": v(-50.8, 202.4) * mm});
            skLineSegment(sketch, "E673", {"start": v(-50.8, 202.4) * mm, "end": v(-50.8, 214.73) * mm});
            skLineSegment(sketch, "E674", {"start": v(-46.04, 214.73) * mm, "end": v(-50.8, 214.73) * mm});
            skLineSegment(sketch, "E675", {"start": v(-46.04, 214.73) * mm, "end": v(-46.04, 227.07) * mm});
            skLineSegment(sketch, "E676", {"start": v(-46.04, 227.07) * mm, "end": v(-50.8, 227.07) * mm});
            skLineSegment(sketch, "E677", {"start": v(-50.8, 227.07) * mm, "end": v(-50.8, 239.4) * mm});
            skLineSegment(sketch, "E678", {"start": v(-46.04, 239.4) * mm, "end": v(-50.8, 239.4) * mm});
            skLineSegment(sketch, "E679", {"start": v(-46.04, 239.4) * mm, "end": v(-46.04, 251.74) * mm});
            skLineSegment(sketch, "E680", {"start": v(-46.04, 251.74) * mm, "end": v(-50.8, 251.74) * mm});
            skLineSegment(sketch, "E681", {"start": v(-50.8, 251.74) * mm, "end": v(-50.8, 264.08) * mm});
            skLineSegment(sketch, "E682", {"start": v(-46.04, 264.08) * mm, "end": v(-50.8, 264.08) * mm});
            skLineSegment(sketch, "E683", {"start": v(-46.04, 264.08) * mm, "end": v(-46.04, 276.42) * mm});
            skLineSegment(sketch, "E684", {"start": v(-46.04, 276.42) * mm, "end": v(-50.8, 276.42) * mm});
            skLineSegment(sketch, "E685", {"start": v(-50.8, 276.42) * mm, "end": v(-50.8, 288.75) * mm});
            skLineSegment(sketch, "E686", {"start": v(-46.04, 288.75) * mm, "end": v(-50.8, 288.75) * mm});
            skLineSegment(sketch, "E687", {"start": v(-46.04, 288.75) * mm, "end": v(-46.04, 301.1) * mm});
            skLineSegment(sketch, "E688", {"start": v(-46.04, 301.1) * mm, "end": v(-50.8, 301.1) * mm});
            skLineSegment(sketch, "E689", {"start": v(-50.8, 301.1) * mm, "end": v(-50.8, 313.43) * mm});
            skLineSegment(sketch, "E690", {"start": v(-46.04, 313.43) * mm, "end": v(-50.8, 313.43) * mm});
            skLineSegment(sketch, "E691", {"start": v(-46.04, 313.43) * mm, "end": v(-46.04, 325.76) * mm});
            skLineSegment(sketch, "E692", {"start": v(-46.04, 325.76) * mm, "end": v(-50.8, 325.76) * mm});
            skLineSegment(sketch, "E693", {"start": v(-50.8, 325.76) * mm, "end": v(-50.8, 338.1) * mm});
            skLineSegment(sketch, "E694", {"start": v(-46.04, 338.1) * mm, "end": v(-50.8, 338.1) * mm});
            skLineSegment(sketch, "E695", {"start": v(-46.04, 338.1) * mm, "end": v(-46.04, 350.44) * mm});
            skLineSegment(sketch, "E696", {"start": v(-46.04, 350.44) * mm, "end": v(-50.8, 350.44) * mm});
            skLineSegment(sketch, "E697", {"start": v(-50.8, 350.44) * mm, "end": v(-50.8, 362.78) * mm});
            skLineSegment(sketch, "E698", {"start": v(-46.04, 362.78) * mm, "end": v(-50.8, 362.78) * mm});
            skLineSegment(sketch, "E699", {"start": v(-46.04, 362.78) * mm, "end": v(-46.04, 375.11) * mm});
            skLineSegment(sketch, "E700", {"start": v(-46.04, 375.11) * mm, "end": v(-50.8, 375.11) * mm});
            skLineSegment(sketch, "E701", {"start": v(-50.8, 375.11) * mm, "end": v(-50.8, 387.45) * mm});
            skLineSegment(sketch, "E702", {"start": v(-46.04, 387.45) * mm, "end": v(-50.8, 387.45) * mm});
            skLineSegment(sketch, "E703", {"start": v(-46.04, 387.45) * mm, "end": v(-46.04, 399.79) * mm});
            skLineSegment(sketch, "E704", {"start": v(-46.04, 399.79) * mm, "end": v(-50.8, 399.79) * mm});
            skLineSegment(sketch, "E705", {"start": v(-50.8, 399.79) * mm, "end": v(-50.8, 412.12) * mm});
            skLineSegment(sketch, "E706", {"start": v(-46.04, 412.12) * mm, "end": v(-50.8, 412.12) * mm});
            skLineSegment(sketch, "E707", {"start": v(-46.04, 412.12) * mm, "end": v(-46.04, 424.46) * mm});
            skLineSegment(sketch, "E708", {"start": v(-46.04, 424.46) * mm, "end": v(-50.8, 424.46) * mm});
            skLineSegment(sketch, "E709", {"start": v(-50.8, 424.46) * mm, "end": v(-50.8, 436.8) * mm});
            skLineSegment(sketch, "E710", {"start": v(46.04, 5) * mm, "end": v(46.04, 17.34) * mm});
            skLineSegment(sketch, "E711", {"start": v(50.8, 17.34) * mm, "end": v(46.04, 17.34) * mm});
            skLineSegment(sketch, "E712", {"start": v(50.8, 17.34) * mm, "end": v(50.8, 29.67) * mm});
            skLineSegment(sketch, "E713", {"start": v(50.8, 29.67) * mm, "end": v(46.04, 29.67) * mm});
            skLineSegment(sketch, "E714", {"start": v(46.04, 29.67) * mm, "end": v(46.04, 42) * mm});
            skLineSegment(sketch, "E715", {"start": v(50.8, 42) * mm, "end": v(46.04, 42) * mm});
            skLineSegment(sketch, "E716", {"start": v(50.8, 42) * mm, "end": v(50.8, 54.35) * mm});
            skLineSegment(sketch, "E717", {"start": v(50.8, 54.35) * mm, "end": v(46.04, 54.35) * mm});
            skLineSegment(sketch, "E718", {"start": v(46.04, 54.35) * mm, "end": v(46.04, 66.68) * mm});
            skLineSegment(sketch, "E719", {"start": v(50.8, 66.68) * mm, "end": v(46.04, 66.68) * mm});
            skLineSegment(sketch, "E720", {"start": v(50.8, 66.68) * mm, "end": v(50.8, 79.02) * mm});
            skLineSegment(sketch, "E721", {"start": v(50.8, 79.02) * mm, "end": v(46.04, 79.02) * mm});
            skLineSegment(sketch, "E722", {"start": v(46.04, 79.02) * mm, "end": v(46.04, 91.36) * mm});
            skLineSegment(sketch, "E723", {"start": v(50.8, 91.36) * mm, "end": v(46.04, 91.36) * mm});
            skLineSegment(sketch, "E724", {"start": v(50.8, 91.36) * mm, "end": v(50.8, 103.7) * mm});
            skLineSegment(sketch, "E725", {"start": v(50.8, 103.7) * mm, "end": v(46.04, 103.7) * mm});
            skLineSegment(sketch, "E726", {"start": v(46.04, 103.7) * mm, "end": v(46.04, 116.03) * mm});
            skLineSegment(sketch, "E727", {"start": v(50.8, 116.03) * mm, "end": v(46.04, 116.03) * mm});
            skLineSegment(sketch, "E728", {"start": v(50.8, 116.03) * mm, "end": v(50.8, 128.37) * mm});
            skLineSegment(sketch, "E729", {"start": v(50.8, 128.37) * mm, "end": v(46.04, 128.37) * mm});
            skLineSegment(sketch, "E730", {"start": v(46.04, 128.37) * mm, "end": v(46.04, 140.7) * mm});
            skLineSegment(sketch, "E731", {"start": v(50.8, 140.7) * mm, "end": v(46.04, 140.7) * mm});
            skLineSegment(sketch, "E732", {"start": v(50.8, 140.7) * mm, "end": v(50.8, 153.04) * mm});
            skLineSegment(sketch, "E733", {"start": v(50.8, 153.04) * mm, "end": v(46.04, 153.04) * mm});
            skLineSegment(sketch, "E734", {"start": v(46.04, 153.04) * mm, "end": v(46.04, 165.38) * mm});
            skLineSegment(sketch, "E735", {"start": v(50.8, 165.38) * mm, "end": v(46.04, 165.38) * mm});
            skLineSegment(sketch, "E736", {"start": v(50.8, 165.38) * mm, "end": v(50.8, 177.72) * mm});
            skLineSegment(sketch, "E737", {"start": v(50.8, 177.72) * mm, "end": v(46.04, 177.72) * mm});
            skLineSegment(sketch, "E738", {"start": v(46.04, 177.72) * mm, "end": v(46.04, 190.06) * mm});
            skLineSegment(sketch, "E739", {"start": v(50.8, 190.06) * mm, "end": v(46.04, 190.06) * mm});
            skLineSegment(sketch, "E740", {"start": v(50.8, 190.06) * mm, "end": v(50.8, 202.4) * mm});
            skLineSegment(sketch, "E741", {"start": v(50.8, 202.4) * mm, "end": v(46.04, 202.4) * mm});
            skLineSegment(sketch, "E742", {"start": v(46.04, 202.4) * mm, "end": v(46.04, 214.73) * mm});
            skLineSegment(sketch, "E743", {"start": v(50.8, 214.73) * mm, "end": v(46.04, 214.73) * mm});
            skLineSegment(sketch, "E744", {"start": v(50.8, 214.73) * mm, "end": v(50.8, 227.07) * mm});
            skLineSegment(sketch, "E745", {"start": v(50.8, 227.07) * mm, "end": v(46.04, 227.07) * mm});
            skLineSegment(sketch, "E746", {"start": v(46.04, 227.07) * mm, "end": v(46.04, 239.4) * mm});
            skLineSegment(sketch, "E747", {"start": v(50.8, 239.4) * mm, "end": v(46.04, 239.4) * mm});
            skLineSegment(sketch, "E748", {"start": v(50.8, 239.4) * mm, "end": v(50.8, 251.74) * mm});
            skLineSegment(sketch, "E749", {"start": v(50.8, 251.74) * mm, "end": v(46.04, 251.74) * mm});
            skLineSegment(sketch, "E750", {"start": v(46.04, 251.74) * mm, "end": v(46.04, 264.08) * mm});
            skLineSegment(sketch, "E751", {"start": v(50.8, 264.08) * mm, "end": v(46.04, 264.08) * mm});
            skLineSegment(sketch, "E752", {"start": v(50.8, 264.08) * mm, "end": v(50.8, 276.42) * mm});
            skLineSegment(sketch, "E753", {"start": v(50.8, 276.42) * mm, "end": v(46.04, 276.42) * mm});
            skLineSegment(sketch, "E754", {"start": v(46.04, 276.42) * mm, "end": v(46.04, 288.75) * mm});
            skLineSegment(sketch, "E755", {"start": v(50.8, 288.75) * mm, "end": v(46.04, 288.75) * mm});
            skLineSegment(sketch, "E756", {"start": v(50.8, 288.75) * mm, "end": v(50.8, 301.1) * mm});
            skLineSegment(sketch, "E757", {"start": v(50.8, 301.1) * mm, "end": v(46.04, 301.1) * mm});
            skLineSegment(sketch, "E758", {"start": v(46.04, 301.1) * mm, "end": v(46.04, 313.43) * mm});
            skLineSegment(sketch, "E759", {"start": v(50.8, 313.43) * mm, "end": v(46.04, 313.43) * mm});
            skLineSegment(sketch, "E760", {"start": v(50.8, 313.43) * mm, "end": v(50.8, 325.76) * mm});
            skLineSegment(sketch, "E761", {"start": v(50.8, 325.76) * mm, "end": v(46.04, 325.76) * mm});
            skLineSegment(sketch, "E762", {"start": v(46.04, 325.76) * mm, "end": v(46.04, 338.1) * mm});
            skLineSegment(sketch, "E763", {"start": v(50.8, 338.1) * mm, "end": v(46.04, 338.1) * mm});
            skLineSegment(sketch, "E764", {"start": v(50.8, 338.1) * mm, "end": v(50.8, 350.44) * mm});
            skLineSegment(sketch, "E765", {"start": v(50.8, 350.44) * mm, "end": v(46.04, 350.44) * mm});
            skLineSegment(sketch, "E766", {"start": v(46.04, 350.44) * mm, "end": v(46.04, 362.78) * mm});
            skLineSegment(sketch, "E767", {"start": v(50.8, 362.78) * mm, "end": v(46.04, 362.78) * mm});
            skLineSegment(sketch, "E768", {"start": v(50.8, 362.78) * mm, "end": v(50.8, 375.11) * mm});
            skLineSegment(sketch, "E769", {"start": v(50.8, 375.11) * mm, "end": v(46.04, 375.11) * mm});
            skLineSegment(sketch, "E770", {"start": v(46.04, 375.11) * mm, "end": v(46.04, 387.45) * mm});
            skLineSegment(sketch, "E771", {"start": v(50.8, 387.45) * mm, "end": v(46.04, 387.45) * mm});
            skLineSegment(sketch, "E772", {"start": v(50.8, 387.45) * mm, "end": v(50.8, 399.79) * mm});
            skLineSegment(sketch, "E773", {"start": v(50.8, 399.79) * mm, "end": v(46.04, 399.79) * mm});
            skLineSegment(sketch, "E774", {"start": v(46.04, 399.79) * mm, "end": v(46.04, 412.12) * mm});
            skLineSegment(sketch, "E775", {"start": v(50.8, 412.12) * mm, "end": v(46.04, 412.12) * mm});
            skLineSegment(sketch, "E776", {"start": v(50.8, 412.12) * mm, "end": v(50.8, 424.46) * mm});
            skLineSegment(sketch, "E777", {"start": v(50.8, 424.46) * mm, "end": v(46.04, 424.46) * mm});
            skLineSegment(sketch, "E778", {"start": v(46.04, 424.46) * mm, "end": v(46.04, 436.8) * mm});
            skLineSegment(sketch, "E779", {"start": v(-46.04, 451.56) * mm, "end": v(-39.51, 451.56) * mm});
            skLineSegment(sketch, "E780", {"start": v(-39.51, 451.56) * mm, "end": v(-39.51, 446.8) * mm});
            skLineSegment(sketch, "E781", {"start": v(-39.51, 446.8) * mm, "end": v(-28.22, 446.8) * mm});
            skLineSegment(sketch, "E782", {"start": v(-28.22, 451.56) * mm, "end": v(-28.22, 446.8) * mm});
            skLineSegment(sketch, "E783", {"start": v(-28.22, 451.56) * mm, "end": v(-16.93, 451.56) * mm});
            skLineSegment(sketch, "E784", {"start": v(-16.93, 451.56) * mm, "end": v(-16.93, 446.8) * mm});
            skLineSegment(sketch, "E785", {"start": v(-16.93, 446.8) * mm, "end": v(-5.65, 446.8) * mm});
            skLineSegment(sketch, "E786", {"start": v(-5.65, 451.56) * mm, "end": v(-5.65, 446.8) * mm});
            skLineSegment(sketch, "E787", {"start": v(-5.65, 451.56) * mm, "end": v(5.64, 451.56) * mm});
            skLineSegment(sketch, "E788", {"start": v(5.64, 451.56) * mm, "end": v(5.64, 446.8) * mm});
            skLineSegment(sketch, "E789", {"start": v(5.64, 446.8) * mm, "end": v(16.93, 446.8) * mm});
            skLineSegment(sketch, "E790", {"start": v(16.93, 451.56) * mm, "end": v(16.93, 446.8) * mm});
            skLineSegment(sketch, "E791", {"start": v(16.93, 451.56) * mm, "end": v(28.22, 451.56) * mm});
            skLineSegment(sketch, "E792", {"start": v(28.22, 451.56) * mm, "end": v(28.22, 446.8) * mm});
            skLineSegment(sketch, "E793", {"start": v(28.22, 446.8) * mm, "end": v(39.51, 446.8) * mm});
            skLineSegment(sketch, "E794", {"start": v(39.51, 451.56) * mm, "end": v(39.51, 446.8) * mm});
            skLineSegment(sketch, "E795", {"start": v(39.51, 451.56) * mm, "end": v(46.04, 451.56) * mm});
            skLineSegment(sketch, "E796", {"start": v(-46.04, 569.04) * mm, "end": v(-39.51, 569.04) * mm});
            skLineSegment(sketch, "E797", {"start": v(-39.51, 573.8) * mm, "end": v(-39.51, 569.04) * mm});
            skLineSegment(sketch, "E798", {"start": v(-39.51, 573.8) * mm, "end": v(-28.22, 573.8) * mm});
            skLineSegment(sketch, "E799", {"start": v(-28.22, 573.8) * mm, "end": v(-28.22, 569.04) * mm});
            skLineSegment(sketch, "E800", {"start": v(-28.22, 569.04) * mm, "end": v(-16.93, 569.04) * mm});
            skLineSegment(sketch, "E801", {"start": v(-16.93, 573.8) * mm, "end": v(-16.93, 569.04) * mm});
            skLineSegment(sketch, "E802", {"start": v(-16.93, 573.8) * mm, "end": v(-5.65, 573.8) * mm});
            skLineSegment(sketch, "E803", {"start": v(-5.65, 573.8) * mm, "end": v(-5.65, 569.04) * mm});
            skLineSegment(sketch, "E804", {"start": v(-5.65, 569.04) * mm, "end": v(5.64, 569.04) * mm});
            skLineSegment(sketch, "E805", {"start": v(5.64, 573.8) * mm, "end": v(5.64, 569.04) * mm});
            skLineSegment(sketch, "E806", {"start": v(5.64, 573.8) * mm, "end": v(16.93, 573.8) * mm});
            skLineSegment(sketch, "E807", {"start": v(16.93, 573.8) * mm, "end": v(16.93, 569.04) * mm});
            skLineSegment(sketch, "E808", {"start": v(16.93, 569.04) * mm, "end": v(28.22, 569.04) * mm});
            skLineSegment(sketch, "E809", {"start": v(28.22, 573.8) * mm, "end": v(28.22, 569.04) * mm});
            skLineSegment(sketch, "E810", {"start": v(28.22, 573.8) * mm, "end": v(39.51, 573.8) * mm});
            skLineSegment(sketch, "E811", {"start": v(39.51, 573.8) * mm, "end": v(39.51, 569.04) * mm});
            skLineSegment(sketch, "E812", {"start": v(39.51, 569.04) * mm, "end": v(46.04, 569.04) * mm});
            skLineSegment(sketch, "E813", {"start": v(-46.04, 451.56) * mm, "end": v(-46.04, 458.34) * mm});
            skLineSegment(sketch, "E814", {"start": v(-46.04, 458.34) * mm, "end": v(-50.8, 458.34) * mm});
            skLineSegment(sketch, "E815", {"start": v(-50.8, 458.34) * mm, "end": v(-50.8, 469.89) * mm});
            skLineSegment(sketch, "E816", {"start": v(-46.04, 469.89) * mm, "end": v(-50.8, 469.89) * mm});
            skLineSegment(sketch, "E817", {"start": v(-46.04, 469.89) * mm, "end": v(-46.04, 481.44) * mm});
            skLineSegment(sketch, "E818", {"start": v(-46.04, 481.44) * mm, "end": v(-50.8, 481.44) * mm});
            skLineSegment(sketch, "E819", {"start": v(-50.8, 481.44) * mm, "end": v(-50.8, 492.98) * mm});
            skLineSegment(sketch, "E820", {"start": v(-46.04, 492.98) * mm, "end": v(-50.8, 492.98) * mm});
            skLineSegment(sketch, "E821", {"start": v(-46.04, 492.98) * mm, "end": v(-46.04, 504.53) * mm});
            skLineSegment(sketch, "E822", {"start": v(-46.04, 504.53) * mm, "end": v(-50.8, 504.53) * mm});
            skLineSegment(sketch, "E823", {"start": v(-50.8, 504.53) * mm, "end": v(-50.8, 516.07) * mm});
            skLineSegment(sketch, "E824", {"start": v(-46.04, 516.07) * mm, "end": v(-50.8, 516.07) * mm});
            skLineSegment(sketch, "E825", {"start": v(-46.04, 516.07) * mm, "end": v(-46.04, 527.62) * mm});
            skLineSegment(sketch, "E826", {"start": v(-46.04, 527.62) * mm, "end": v(-50.8, 527.62) * mm});
            skLineSegment(sketch, "E827", {"start": v(-50.8, 527.62) * mm, "end": v(-50.8, 539.16) * mm});
            skLineSegment(sketch, "E828", {"start": v(-46.04, 539.16) * mm, "end": v(-50.8, 539.16) * mm});
            skLineSegment(sketch, "E829", {"start": v(-46.04, 539.16) * mm, "end": v(-46.04, 550.7) * mm});
            skLineSegment(sketch, "E830", {"start": v(-46.04, 550.7) * mm, "end": v(-50.8, 550.7) * mm});
            skLineSegment(sketch, "E831", {"start": v(-50.8, 550.7) * mm, "end": v(-50.8, 562.25) * mm});
            skLineSegment(sketch, "E832", {"start": v(-46.04, 562.25) * mm, "end": v(-50.8, 562.25) * mm});
            skLineSegment(sketch, "E833", {"start": v(-46.04, 562.25) * mm, "end": v(-46.04, 569.04) * mm});
            skLineSegment(sketch, "E834", {"start": v(46.04, 451.56) * mm, "end": v(46.04, 458.34) * mm});
            skLineSegment(sketch, "E835", {"start": v(50.8, 458.34) * mm, "end": v(46.04, 458.34) * mm});
            skLineSegment(sketch, "E836", {"start": v(50.8, 458.34) * mm, "end": v(50.8, 469.89) * mm});
            skLineSegment(sketch, "E837", {"start": v(50.8, 469.89) * mm, "end": v(46.04, 469.89) * mm});
            skLineSegment(sketch, "E838", {"start": v(46.04, 469.89) * mm, "end": v(46.04, 481.44) * mm});
            skLineSegment(sketch, "E839", {"start": v(50.8, 481.44) * mm, "end": v(46.04, 481.44) * mm});
            skLineSegment(sketch, "E840", {"start": v(50.8, 481.44) * mm, "end": v(50.8, 492.98) * mm});
            skLineSegment(sketch, "E841", {"start": v(50.8, 492.98) * mm, "end": v(46.04, 492.98) * mm});
            skLineSegment(sketch, "E842", {"start": v(46.04, 492.98) * mm, "end": v(46.04, 504.53) * mm});
            skLineSegment(sketch, "E843", {"start": v(50.8, 504.53) * mm, "end": v(46.04, 504.53) * mm});
            skLineSegment(sketch, "E844", {"start": v(50.8, 504.53) * mm, "end": v(50.8, 516.07) * mm});
            skLineSegment(sketch, "E845", {"start": v(50.8, 516.07) * mm, "end": v(46.04, 516.07) * mm});
            skLineSegment(sketch, "E846", {"start": v(46.04, 516.07) * mm, "end": v(46.04, 527.62) * mm});
            skLineSegment(sketch, "E847", {"start": v(50.8, 527.62) * mm, "end": v(46.04, 527.62) * mm});
            skLineSegment(sketch, "E848", {"start": v(50.8, 527.62) * mm, "end": v(50.8, 539.16) * mm});
            skLineSegment(sketch, "E849", {"start": v(50.8, 539.16) * mm, "end": v(46.04, 539.16) * mm});
            skLineSegment(sketch, "E850", {"start": v(46.04, 539.16) * mm, "end": v(46.04, 550.7) * mm});
            skLineSegment(sketch, "E851", {"start": v(50.8, 550.7) * mm, "end": v(46.04, 550.7) * mm});
            skLineSegment(sketch, "E852", {"start": v(50.8, 550.7) * mm, "end": v(50.8, 562.25) * mm});
            skLineSegment(sketch, "E853", {"start": v(50.8, 562.25) * mm, "end": v(46.04, 562.25) * mm});
            skLineSegment(sketch, "E854", {"start": v(46.04, 562.25) * mm, "end": v(46.04, 569.04) * mm});
            skLineSegment(sketch, "E855", {"start": v(0, -573.8) * mm, "end": v(0, -142) * mm, "construction": true});
            skLineSegment(sketch, "E856", {"start": v(0, -357.9) * mm, "end": v(120.84, -357.9) * mm, "construction": true});
            skPoint(sketch, "E856.endSnap0", {"position": v(0, -357.9) * mm});
            skLineSegment(sketch, "E857", {"start": v(120.84, -357.9) * mm, "end": v(-93.73, -357.9) * mm, "construction": true});
            skLineSegment(sketch, "E858", {"start": v(0, -40.07) * mm, "end": v(0, 391.73) * mm, "construction": true});
            skLineSegment(sketch, "E859", {"start": v(0, 213.44) * mm, "end": v(118.16, 213.44) * mm, "construction": true});
            skPoint(sketch, "E859.startSnap0", {"position": v(0, 175.83) * mm});
            skLineSegment(sketch, "E860", {"start": v(0, 213.44) * mm, "end": v(-118.45, 213.44) * mm, "construction": true});
            skCircle(sketch, "E861", {"center": v(0, 381.88) * mm, "radius": 30.21 * mm});
            skCircle(sketch, "E862", {"center": v(0, 45) * mm, "radius": 30.21 * mm});
            skLineSegment(sketch, "E863", {"start": v(-5.65, 436.8) * mm, "end": v(5.64, 436.8) * mm});
            skLineSegment(sketch, "E864", {"start": v(-5.65, 5) * mm, "end": v(5.64, 5) * mm});
            skCircle(sketch, "E865", {"center": v(0, -189.51) * mm, "radius": 30.21 * mm});
            skCircle(sketch, "E866", {"center": v(0, -526.3) * mm, "radius": 30.21 * mm});
            skLineSegment(sketch, "E867", {"start": v(65.56, 90.07) * mm, "end": v(60.8, 90.07) * mm});
            skSolve(sketch);
        }
        {
            var Q0;
            Q0 = qSketchRegion(id + "F0", true);
            extrude(context, id + "F1", {"entities" : qUnion([Q0]), "depth" : 25.4 * mm});
        }
    });
